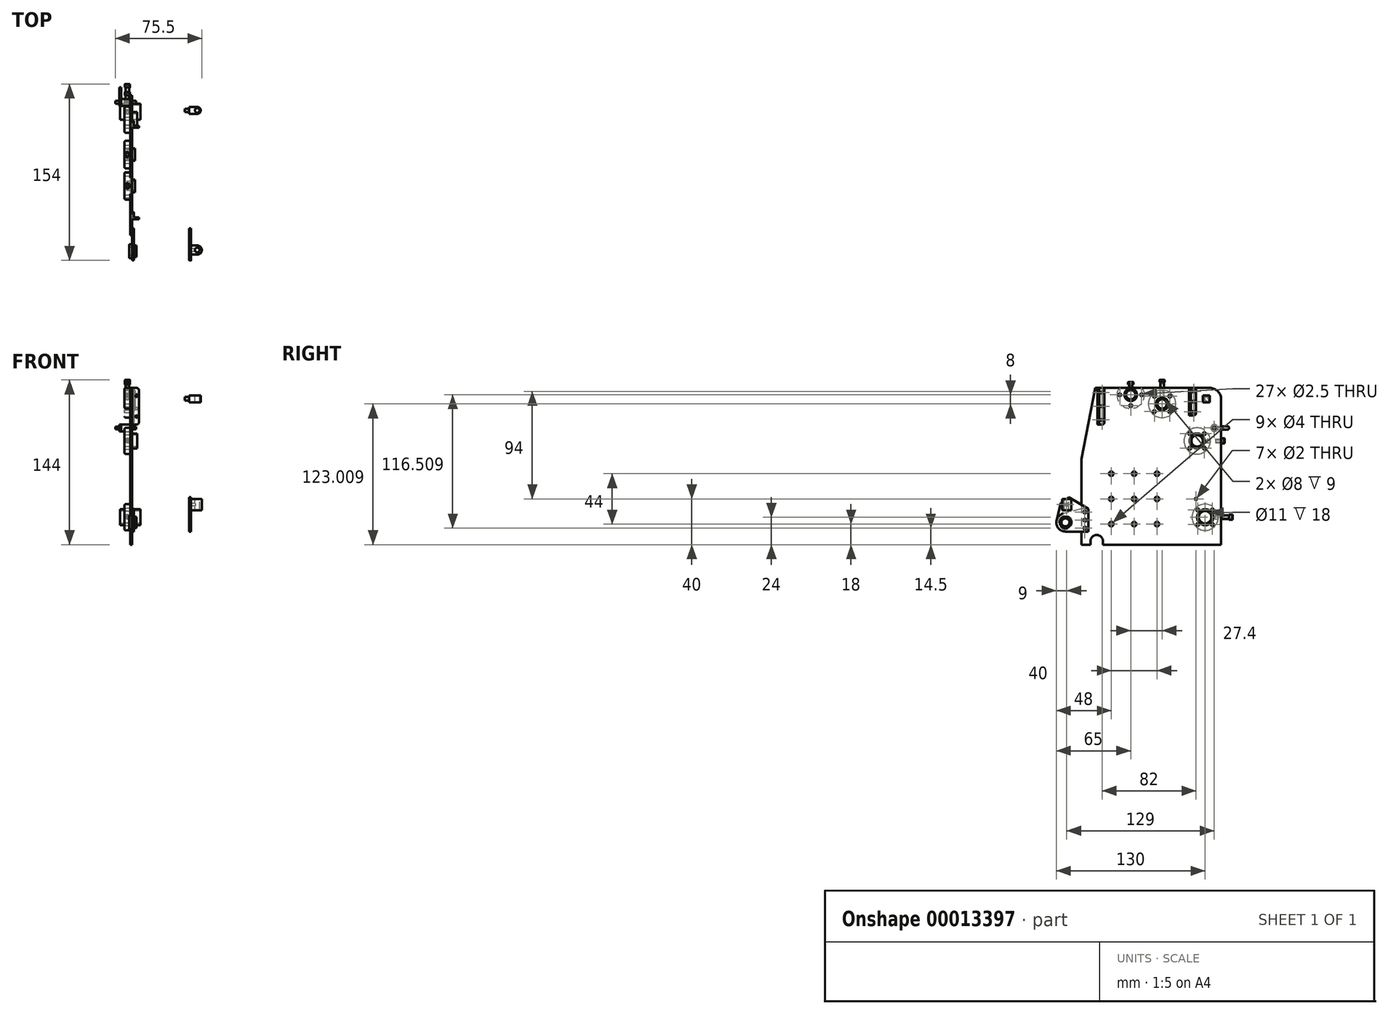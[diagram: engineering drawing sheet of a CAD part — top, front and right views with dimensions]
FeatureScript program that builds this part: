
annotation { "Feature Type Name" : "Feature", "Feature Type Description" : "" }
export const myFeature = defineFeature(function(context is Context, id is Id, definition is map)
    precondition{}
    {
        {
            var Q0;
            Q0=qCreatedBy(makeId("Right.planeOp"),FACE);
            var sketch = newSketch(context, id + "F0", { "sketchPlane" : qUnion([Q0])});
            skLineSegment(sketch, "E0", {"start": v(0, 75) * mm, "end": v(0, 0) * mm});
            skLineSegment(sketch, "E1", {"start": v(0, 0) * mm, "end": v(122, 0) * mm});
            skLineSegment(sketch, "E2", {"start": v(122, 0) * mm, "end": v(122, 127) * mm});
            skLineSegment(sketch, "E3", {"start": v(112, 137) * mm, "end": v(12, 137) * mm});
            skLineSegment(sketch, "E4", {"start": v(12, 137) * mm, "end": v(0, 75) * mm});
            skLineSegment(sketch, "E5", {"start": v(13.3, 0) * mm, "end": v(13.3, 3) * mm, "construction": true});
            skLineSegment(sketch, "E6", {"start": v(108, 0) * mm, "end": v(108, 24) * mm, "construction": true});
            skLineSegment(sketch, "E7", {"start": v(101, 0) * mm, "end": v(101, 90.7) * mm, "construction": true});
            skLineSegment(sketch, "E8", {"start": v(122, 40) * mm, "end": v(100, 40) * mm, "construction": true});
            skLineSegment(sketch, "E9", {"start": v(109, 137) * mm, "end": v(109, 127.5) * mm, "construction": true});
            skLineSegment(sketch, "E10", {"start": v(98, 137) * mm, "end": v(98, 134) * mm, "construction": true});
            skLineSegment(sketch, "E11", {"start": v(70.4, 137) * mm, "end": v(70.4, 101.73) * mm, "construction": true});
            skLineSegment(sketch, "E12", {"start": v(43, 137) * mm, "end": v(43, 131) * mm, "construction": true});
            skLineSegment(sketch, "E13", {"start": v(18, 137) * mm, "end": v(18, 133) * mm, "construction": true});
            skCircle(sketch, "E14", {"center": v(101, 90.7) * mm, "radius": 44.5 * mm, "construction": true});
            skCircle(sketch, "E15", {"center": v(70.4, 123) * mm, "radius": 5.5 * mm});
            skLineSegment(sketch, "E16", {"start": v(70.4, 123) * mm, "end": v(53.04, 123) * mm, "construction": true});
            skCircle(sketch, "E17", {"center": v(43, 131) * mm, "radius": 5.5 * mm});
            skCircle(sketch, "E18", {"center": v(101, 90.7) * mm, "radius": 6.5 * mm});
            skCircle(sketch, "E19", {"center": v(13.3, 3) * mm, "radius": 5.5 * mm});
            skCircle(sketch, "E20", {"center": v(108, 24) * mm, "radius": 7 * mm});
            skCircle(sketch, "E21", {"center": v(18, 133) * mm, "radius": 1 * mm});
            skCircle(sketch, "E22", {"center": v(98, 134) * mm, "radius": 1 * mm});
            skCircle(sketch, "E23", {"center": v(109, 127.5) * mm, "radius": 1.5 * mm});
            skCircle(sketch, "E24", {"center": v(100, 40) * mm, "radius": 1 * mm});
            skCircle(sketch, "E25.0.1.0", {"center": v(18, 121) * mm, "radius": 1 * mm});
            skCircle(sketch, "E25.0.2.0", {"center": v(18, 109) * mm, "radius": 1 * mm});
            skLineSegment(sketch, "E25.direction1", {"start": v(18, 133) * mm, "end": v(6, 133) * mm, "construction": true});
            skLineSegment(sketch, "E25.direction2", {"start": v(18, 133) * mm, "end": v(18, 121) * mm, "construction": true});
            skCircle(sketch, "E26.0.1.0", {"center": v(98, 125) * mm, "radius": 1 * mm});
            skCircle(sketch, "E26.0.2.0", {"center": v(98, 116) * mm, "radius": 1 * mm});
            skLineSegment(sketch, "E26.direction1", {"start": v(98, 134) * mm, "end": v(123, 134) * mm, "construction": true});
            skLineSegment(sketch, "E26.direction2", {"start": v(98, 134) * mm, "end": v(98, 125) * mm, "construction": true});
            skLineSegment(sketch, "E27", {"start": v(122, 102) * mm, "end": v(116, 102) * mm, "construction": true});
            skCircle(sketch, "E28", {"center": v(116, 102) * mm, "radius": 1.25 * mm});
            skLineSegment(sketch, "E29", {"start": v(43, 131) * mm, "end": v(33.5, 131) * mm, "construction": true});
            skCircle(sketch, "E30", {"center": v(33.5, 131) * mm, "radius": 1.25 * mm});
            skLineSegment(sketch, "E31", {"start": v(70.4, 123) * mm, "end": v(63.68, 129.73) * mm, "construction": true});
            skCircle(sketch, "E32", {"center": v(63.68, 129.73) * mm, "radius": 1.25 * mm});
            skCircle(sketch, "E33.1.0", {"center": v(63.68, 116.3) * mm, "radius": 1.25 * mm});
            skCircle(sketch, "E33.2.0", {"center": v(77.12, 116.3) * mm, "radius": 1.25 * mm});
            skCircle(sketch, "E33.3.0", {"center": v(77.12, 129.73) * mm, "radius": 1.25 * mm});
            skLineSegment(sketch, "E34", {"start": v(101, 90.7) * mm, "end": v(94.64, 84.34) * mm, "construction": true});
            skCircle(sketch, "E35", {"center": v(94.64, 84.34) * mm, "radius": 1.25 * mm});
            skCircle(sketch, "E36.1.0", {"center": v(107.36, 84.34) * mm, "radius": 1.25 * mm});
            skCircle(sketch, "E36.2.0", {"center": v(107.36, 97.06) * mm, "radius": 1.25 * mm});
            skCircle(sketch, "E36.3.0", {"center": v(94.64, 97.06) * mm, "radius": 1.25 * mm});
            skLineSegment(sketch, "E37", {"start": v(108, 24) * mm, "end": v(114.36, 17.64) * mm, "construction": true});
            skCircle(sketch, "E38", {"center": v(114.36, 17.64) * mm, "radius": 1.25 * mm});
            skCircle(sketch, "E39.1.0", {"center": v(114.36, 30.36) * mm, "radius": 1.25 * mm});
            skCircle(sketch, "E39.2.0", {"center": v(101.64, 30.36) * mm, "radius": 1.25 * mm});
            skCircle(sketch, "E39.3.0", {"center": v(101.64, 17.64) * mm, "radius": 1.25 * mm});
            skLineSegment(sketch, "E40", {"start": v(7.8, 3) * mm, "end": v(7.8, 0) * mm});
            skLineSegment(sketch, "E41", {"start": v(18.8, 3) * mm, "end": v(18.8, 0) * mm});
            skLineSegment(sketch, "E42", {"start": v(66, 0) * mm, "end": v(66, 18) * mm, "construction": true});
            skCircle(sketch, "E43", {"center": v(66, 18) * mm, "radius": 2 * mm});
            skCircle(sketch, "E44.0.1.0", {"center": v(66, 40) * mm, "radius": 2 * mm});
            skCircle(sketch, "E44.0.2.0", {"center": v(66, 62) * mm, "radius": 2 * mm});
            skCircle(sketch, "E44.1.0.0", {"center": v(46, 18) * mm, "radius": 2 * mm});
            skCircle(sketch, "E44.1.1.0", {"center": v(46, 40) * mm, "radius": 2 * mm});
            skCircle(sketch, "E44.1.2.0", {"center": v(46, 62) * mm, "radius": 2 * mm});
            skCircle(sketch, "E44.2.0.0", {"center": v(26, 18) * mm, "radius": 2 * mm});
            skCircle(sketch, "E44.2.1.0", {"center": v(26, 40) * mm, "radius": 2 * mm});
            skCircle(sketch, "E44.2.2.0", {"center": v(26, 62) * mm, "radius": 2 * mm});
            skLineSegment(sketch, "E44.direction1", {"start": v(66, 18) * mm, "end": v(46, 18) * mm, "construction": true});
            skLineSegment(sketch, "E44.direction2", {"start": v(66, 18) * mm, "end": v(66, 40) * mm, "construction": true});
            skLineSegment(sketch, "E45", {"start": v(0, 14.5) * mm, "end": v(3, 14.5) * mm, "construction": true});
            skCircle(sketch, "E46", {"center": v(3, 14.5) * mm, "radius": 1.25 * mm});
            skCircle(sketch, "E47.0.1.0", {"center": v(3, 21.5) * mm, "radius": 1.25 * mm});
            skCircle(sketch, "E47.0.2.0", {"center": v(3, 28.5) * mm, "radius": 1.25 * mm});
            skLineSegment(sketch, "E47.direction1", {"start": v(3, 14.5) * mm, "end": v(3, 14.5) * mm});
            skLineSegment(sketch, "E47.direction2", {"start": v(3, 14.5) * mm, "end": v(3, 21.5) * mm, "construction": true});
            skPoint(sketch, "E48.visualSharp", {"position": v(122, 137) * mm});
            skArc(sketch, "E48.filletArc", {"start": v(122, 127) * mm, "mid": v(119.07, 134.07) * mm, "end": v(112, 137) * mm});
            skCircle(sketch, "E49.1.0", {"center": v(43, 121.5) * mm, "radius": 1.25 * mm});
            skCircle(sketch, "E49.2.0", {"center": v(52.5, 131) * mm, "radius": 1.25 * mm});
            skCircle(sketch, "E49.3.0", {"center": v(43, 140.5) * mm, "radius": 1.25 * mm});
            skSolve(sketch);
        }
        {
            var Q0;
            {var subQ2=sQuery(id+"F0.wireOp",EDGE,"E0");Q0=makeQuery(id+"F0.imprint","IMPRINT",FACE,{"disambiguationData":[TD([[makeQuery(id+"F0.imprint","IMPRINT",EDGE,{"derivedFrom":subQ2}),1.0]])]});}
            extrude(context, id + "F1", {"entities" : qUnion([Q0]), "depth" : 1.5 * mm});
        }
        {
            var Q0;
            Q0=makeQuery(id+"F1.opExtrude","CAP_FACE",FACE,{"disambiguationData":[OSD([sQuery(id+"F0.wireOp",EDGE,"E0"),sQuery(id+"F0.wireOp",EDGE,"E1"),sQuery(id+"F0.wireOp",EDGE,"E2"),sQuery(id+"F0.wireOp",EDGE,"E3"),sQuery(id+"F0.wireOp",EDGE,"E4"),sQuery(id+"F0.wireOp",EDGE,"E15"),sQuery(id+"F0.wireOp",EDGE,"E17"),sQuery(id+"F0.wireOp",EDGE,"E18"),sQuery(id+"F0.wireOp",EDGE,"E19"),sQuery(id+"F0.wireOp",EDGE,"E20"),sQuery(id+"F0.wireOp",EDGE,"E21"),sQuery(id+"F0.wireOp",EDGE,"E22"),sQuery(id+"F0.wireOp",EDGE,"E23"),sQuery(id+"F0.wireOp",EDGE,"E24"),sQuery(id+"F0.wireOp",EDGE,"E25.0.1.0"),sQuery(id+"F0.wireOp",EDGE,"E25.0.2.0"),sQuery(id+"F0.wireOp",EDGE,"E26.0.1.0"),sQuery(id+"F0.wireOp",EDGE,"E26.0.2.0"),sQuery(id+"F0.wireOp",EDGE,"E28"),sQuery(id+"F0.wireOp",EDGE,"E30"),sQuery(id+"F0.wireOp",EDGE,"E32"),sQuery(id+"F0.wireOp",EDGE,"E33.1.0"),sQuery(id+"F0.wireOp",EDGE,"E33.2.0"),sQuery(id+"F0.wireOp",EDGE,"E33.3.0"),sQuery(id+"F0.wireOp",EDGE,"E35"),sQuery(id+"F0.wireOp",EDGE,"E36.1.0"),sQuery(id+"F0.wireOp",EDGE,"E36.2.0"),sQuery(id+"F0.wireOp",EDGE,"E36.3.0"),sQuery(id+"F0.wireOp",EDGE,"E38"),sQuery(id+"F0.wireOp",EDGE,"E39.1.0"),sQuery(id+"F0.wireOp",EDGE,"E39.2.0"),sQuery(id+"F0.wireOp",EDGE,"E39.3.0"),sQuery(id+"F0.wireOp",EDGE,"E40"),sQuery(id+"F0.wireOp",EDGE,"E41"),sQuery(id+"F0.wireOp",EDGE,"E43"),sQuery(id+"F0.wireOp",EDGE,"E44.0.1.0"),sQuery(id+"F0.wireOp",EDGE,"E44.0.2.0"),sQuery(id+"F0.wireOp",EDGE,"E44.1.0.0"),sQuery(id+"F0.wireOp",EDGE,"E44.1.1.0"),sQuery(id+"F0.wireOp",EDGE,"E44.1.2.0"),sQuery(id+"F0.wireOp",EDGE,"E44.2.0.0"),sQuery(id+"F0.wireOp",EDGE,"E44.2.1.0"),sQuery(id+"F0.wireOp",EDGE,"E44.2.2.0"),sQuery(id+"F0.wireOp",EDGE,"E46"),sQuery(id+"F0.wireOp",EDGE,"E47.0.1.0"),sQuery(id+"F0.wireOp",EDGE,"E47.0.2.0"),sQuery(id+"F0.wireOp",EDGE,"E48.filletArc"),sQuery(id+"F0.wireOp",EDGE,"E49.1.0"),sQuery(id+"F0.wireOp",EDGE,"E49.2.0")])],"isStart":false});
            var sketch = newSketch(context, id + "F2", { "sketchPlane" : qUnion([Q0])});
            skCircle(sketch, "E50.0", {"center": v(18, 133) * mm, "radius": 1 * mm});
            skCircle(sketch, "E50.1", {"center": v(18, 121) * mm, "radius": 1 * mm});
            skCircle(sketch, "E50.2", {"center": v(18, 109) * mm, "radius": 1 * mm});
            skLineSegment(sketch, "E51.bottom", {"start": v(14, 137) * mm, "end": v(18, 137) * mm});
            skLineSegment(sketch, "E51.top", {"start": v(14, 105) * mm, "end": v(18, 105) * mm});
            skLineSegment(sketch, "E51.left", {"start": v(14, 137) * mm, "end": v(14, 105) * mm});
            skLineSegment(sketch, "E51.right", {"start": v(20, 135) * mm, "end": v(20, 107) * mm});
            skLineSegment(sketch, "E52", {"start": v(15.5, 137) * mm, "end": v(15.5, 105) * mm});
            skPoint(sketch, "E53.visualSharp", {"position": v(20, 137) * mm});
            skArc(sketch, "E53.filletArc", {"start": v(20, 135) * mm, "mid": v(19.41, 136.41) * mm, "end": v(18, 137) * mm});
            skPoint(sketch, "E54.visualSharp", {"position": v(20, 105) * mm});
            skArc(sketch, "E54.filletArc", {"start": v(18, 105) * mm, "mid": v(19.41, 105.59) * mm, "end": v(20, 107) * mm});
            skSolve(sketch);
        }
        {
            var Q0;
            {var subQ1=sQuery(id+"F2.wireOp",EDGE,"E51.left");Q0=makeQuery(id+"F2.imprint","IMPRINT",FACE,{"disambiguationData":[TD([[makeQuery(id+"F2.imprint","IMPRINT",EDGE,{"derivedFrom":subQ1}),1.0]])]});}
            extrude(context, id + "F3", {"entities" : qUnion([Q0]), "depth" : 6 * mm});
        }
        {
            var Q0;
            Q0=makeQuery(id+"F2.imprint","IMPRINT",FACE,{"disambiguationData":[TD([[makeQuery(id+"F2.imprint","IMPRINT",EDGE,{"derivedFrom":sQuery(id+"F2.wireOp",EDGE,"E50.0")}),-1.0]])]});
            extrude(context, id + "F4", {"entities" : qUnion([Q0]), "operationType" : NewBodyOperationType.ADD, "depth" : 1.5 * mm});
        }
        {
            var Q0;
            Q0=makeQuery(id+"F3.opExtrude","SWEPT_FACE",FACE,{"disambiguationData":[OSD([sQuery(id+"F2.wireOp",EDGE,"E51.left")])]});
            var sketch = newSketch(context, id + "F5", { "sketchPlane" : qUnion([Q0])});
            skLineSegment(sketch, "E55", {"start": v(5.5, 137) * mm, "end": v(5.5, 105) * mm, "construction": true});
            skLineSegment(sketch, "E56", {"start": v(5.5, 130) * mm, "end": v(7.5, 130) * mm, "construction": true});
            skLineSegment(sketch, "E57", {"start": v(5.5, 112) * mm, "end": v(7.5, 112) * mm, "construction": true});
            skCircle(sketch, "E58", {"center": v(5.5, 130) * mm, "radius": 1 * mm});
            skCircle(sketch, "E59", {"center": v(5.5, 112) * mm, "radius": 1 * mm});
            skSolve(sketch);
        }
        {
            var Q0;
            Q0=makeQuery(id+"F5.imprint","IMPRINT",FACE,{"disambiguationData":[TD([[makeQuery(id+"F5.imprint","IMPRINT",EDGE,{"derivedFrom":sQuery(id+"F5.wireOp",EDGE,"E58")}),1.0]])]});
            var Q1;
            Q1=makeQuery(id+"F5.imprint","IMPRINT",FACE,{"disambiguationData":[TD([[makeQuery(id+"F5.imprint","IMPRINT",EDGE,{"derivedFrom":sQuery(id+"F5.wireOp",EDGE,"E59")}),1.0]])]});
            extrude(context, id + "F6", {"entities" : qUnion([Q0, Q1]), "operationType" : NewBodyOperationType.REMOVE, "oppositeDirection" : true, "depth" : 1.5 * mm});
        }
        {
            var Q0;
            Q0=makeQuery(id+"F3.opExtrude","CAP_EDGE",EDGE,{"disambiguationData":[OSD([sQuery(id+"F2.wireOp",EDGE,"E51.bottom")])],"isStart":false});
            var Q1;
            Q1=makeQuery(id+"F3.opExtrude","CAP_EDGE",EDGE,{"disambiguationData":[OSD([sQuery(id+"F2.wireOp",EDGE,"E51.top")])],"isStart":false});
            fillet(context, id + "F7", {"entities" : qUnion([Q0, Q1]), "radius" : 2 * mm, "tangentPropagation" : true, "allowEdgeOverflow" : false});
        }
        {
            var Q0;
            Q0=makeQuery(id+"F1.opExtrude","CAP_FACE",FACE,{"disambiguationData":[OSD([sQuery(id+"F0.wireOp",EDGE,"E0"),sQuery(id+"F0.wireOp",EDGE,"E1"),sQuery(id+"F0.wireOp",EDGE,"E2"),sQuery(id+"F0.wireOp",EDGE,"E3"),sQuery(id+"F0.wireOp",EDGE,"E4"),sQuery(id+"F0.wireOp",EDGE,"E15"),sQuery(id+"F0.wireOp",EDGE,"E17"),sQuery(id+"F0.wireOp",EDGE,"E18"),sQuery(id+"F0.wireOp",EDGE,"E19"),sQuery(id+"F0.wireOp",EDGE,"E20"),sQuery(id+"F0.wireOp",EDGE,"E21"),sQuery(id+"F0.wireOp",EDGE,"E22"),sQuery(id+"F0.wireOp",EDGE,"E23"),sQuery(id+"F0.wireOp",EDGE,"E24"),sQuery(id+"F0.wireOp",EDGE,"E25.0.1.0"),sQuery(id+"F0.wireOp",EDGE,"E25.0.2.0"),sQuery(id+"F0.wireOp",EDGE,"E26.0.1.0"),sQuery(id+"F0.wireOp",EDGE,"E26.0.2.0"),sQuery(id+"F0.wireOp",EDGE,"E28"),sQuery(id+"F0.wireOp",EDGE,"E30"),sQuery(id+"F0.wireOp",EDGE,"E32"),sQuery(id+"F0.wireOp",EDGE,"E33.1.0"),sQuery(id+"F0.wireOp",EDGE,"E33.2.0"),sQuery(id+"F0.wireOp",EDGE,"E33.3.0"),sQuery(id+"F0.wireOp",EDGE,"E35"),sQuery(id+"F0.wireOp",EDGE,"E36.1.0"),sQuery(id+"F0.wireOp",EDGE,"E36.2.0"),sQuery(id+"F0.wireOp",EDGE,"E36.3.0"),sQuery(id+"F0.wireOp",EDGE,"E38"),sQuery(id+"F0.wireOp",EDGE,"E39.1.0"),sQuery(id+"F0.wireOp",EDGE,"E39.2.0"),sQuery(id+"F0.wireOp",EDGE,"E39.3.0"),sQuery(id+"F0.wireOp",EDGE,"E40"),sQuery(id+"F0.wireOp",EDGE,"E41"),sQuery(id+"F0.wireOp",EDGE,"E43"),sQuery(id+"F0.wireOp",EDGE,"E44.0.1.0"),sQuery(id+"F0.wireOp",EDGE,"E44.0.2.0"),sQuery(id+"F0.wireOp",EDGE,"E44.1.0.0"),sQuery(id+"F0.wireOp",EDGE,"E44.1.1.0"),sQuery(id+"F0.wireOp",EDGE,"E44.1.2.0"),sQuery(id+"F0.wireOp",EDGE,"E44.2.0.0"),sQuery(id+"F0.wireOp",EDGE,"E44.2.1.0"),sQuery(id+"F0.wireOp",EDGE,"E44.2.2.0"),sQuery(id+"F0.wireOp",EDGE,"E46"),sQuery(id+"F0.wireOp",EDGE,"E47.0.1.0"),sQuery(id+"F0.wireOp",EDGE,"E47.0.2.0"),sQuery(id+"F0.wireOp",EDGE,"E48.filletArc"),sQuery(id+"F0.wireOp",EDGE,"E49.1.0"),sQuery(id+"F0.wireOp",EDGE,"E49.2.0")])],"isStart":false});
            var sketch = newSketch(context, id + "F8", { "sketchPlane" : qUnion([Q0])});
            skCircle(sketch, "E60.0", {"center": v(98, 134) * mm, "radius": 1 * mm});
            skCircle(sketch, "E60.1", {"center": v(98, 125) * mm, "radius": 1 * mm});
            skCircle(sketch, "E60.2", {"center": v(98, 116) * mm, "radius": 1 * mm});
            skLineSegment(sketch, "E61.bottom", {"start": v(98, 137) * mm, "end": v(94, 137) * mm});
            skLineSegment(sketch, "E61.top", {"start": v(98, 113) * mm, "end": v(94, 113) * mm});
            skLineSegment(sketch, "E61.left", {"start": v(100, 135) * mm, "end": v(100, 115) * mm});
            skLineSegment(sketch, "E61.right", {"start": v(94, 137) * mm, "end": v(94, 113) * mm});
            skLineSegment(sketch, "E62", {"start": v(95.5, 137) * mm, "end": v(95.5, 113) * mm});
            skPoint(sketch, "E63.visualSharp", {"position": v(100, 113) * mm});
            skArc(sketch, "E63.filletArc", {"start": v(98, 113) * mm, "mid": v(99.41, 113.59) * mm, "end": v(100, 115) * mm});
            skPoint(sketch, "E64.visualSharp", {"position": v(100, 137) * mm});
            skArc(sketch, "E64.filletArc", {"start": v(100, 135) * mm, "mid": v(99.41, 136.41) * mm, "end": v(98, 137) * mm});
            skSolve(sketch);
        }
        {
            var Q0;
            {var subQ1=sQuery(id+"F8.wireOp",EDGE,"E61.right");Q0=makeQuery(id+"F8.imprint","IMPRINT",FACE,{"disambiguationData":[TD([[makeQuery(id+"F8.imprint","IMPRINT",EDGE,{"derivedFrom":subQ1}),1.0]])]});}
            extrude(context, id + "F9", {"entities" : qUnion([Q0]), "depth" : 6 * mm});
        }
        {
            var Q0;
            Q0=makeQuery(id+"F8.imprint","IMPRINT",FACE,{"disambiguationData":[TD([[makeQuery(id+"F8.imprint","IMPRINT",EDGE,{"derivedFrom":sQuery(id+"F8.wireOp",EDGE,"E60.0")}),-1.0]])]});
            extrude(context, id + "F10", {"entities" : qUnion([Q0]), "operationType" : NewBodyOperationType.ADD, "depth" : 1.5 * mm});
        }
        {
            var Q0;
            Q0=makeQuery(id+"F9.opExtrude","SWEPT_FACE",FACE,{"disambiguationData":[OSD([sQuery(id+"F8.wireOp",EDGE,"E61.right")])]});
            var sketch = newSketch(context, id + "F11", { "sketchPlane" : qUnion([Q0])});
            skLineSegment(sketch, "E65", {"start": v(5.5, 137) * mm, "end": v(5.5, 113) * mm, "construction": true});
            skLineSegment(sketch, "E66", {"start": v(5.5, 131) * mm, "end": v(7.5, 131) * mm, "construction": true});
            skLineSegment(sketch, "E67", {"start": v(5.5, 119) * mm, "end": v(7.5, 119) * mm, "construction": true});
            skCircle(sketch, "E68", {"center": v(5.5, 131) * mm, "radius": 1 * mm});
            skCircle(sketch, "E69", {"center": v(5.5, 119) * mm, "radius": 1 * mm});
            skSolve(sketch);
        }
        {
            var Q0;
            Q0=makeQuery(id+"F11.imprint","IMPRINT",FACE,{"disambiguationData":[TD([[makeQuery(id+"F11.imprint","IMPRINT",EDGE,{"derivedFrom":sQuery(id+"F11.wireOp",EDGE,"E68")}),1.0]])]});
            var Q1;
            Q1=makeQuery(id+"F11.imprint","IMPRINT",FACE,{"disambiguationData":[TD([[makeQuery(id+"F11.imprint","IMPRINT",EDGE,{"derivedFrom":sQuery(id+"F11.wireOp",EDGE,"E69")}),1.0]])]});
            extrude(context, id + "F12", {"entities" : qUnion([Q0, Q1]), "operationType" : NewBodyOperationType.REMOVE, "oppositeDirection" : true, "depth" : 1.5 * mm});
        }
        {
            var Q0;
            Q0=makeQuery(id+"F9.opExtrude","CAP_EDGE",EDGE,{"disambiguationData":[OSD([sQuery(id+"F8.wireOp",EDGE,"E61.bottom")])],"isStart":false});
            var Q1;
            Q1=makeQuery(id+"F9.opExtrude","CAP_EDGE",EDGE,{"disambiguationData":[OSD([sQuery(id+"F8.wireOp",EDGE,"E61.top")])],"isStart":false});
            fillet(context, id + "F13", {"entities" : qUnion([Q0, Q1]), "radius" : 2 * mm, "tangentPropagation" : true, "allowEdgeOverflow" : false});
        }
        {
            var Q0;
            Q0=makeQuery(id+"F1.opExtrude","CAP_FACE",FACE,{"disambiguationData":[OSD([sQuery(id+"F0.wireOp",EDGE,"E0"),sQuery(id+"F0.wireOp",EDGE,"E1"),sQuery(id+"F0.wireOp",EDGE,"E2"),sQuery(id+"F0.wireOp",EDGE,"E3"),sQuery(id+"F0.wireOp",EDGE,"E4"),sQuery(id+"F0.wireOp",EDGE,"E15"),sQuery(id+"F0.wireOp",EDGE,"E17"),sQuery(id+"F0.wireOp",EDGE,"E18"),sQuery(id+"F0.wireOp",EDGE,"E19"),sQuery(id+"F0.wireOp",EDGE,"E20"),sQuery(id+"F0.wireOp",EDGE,"E21"),sQuery(id+"F0.wireOp",EDGE,"E22"),sQuery(id+"F0.wireOp",EDGE,"E23"),sQuery(id+"F0.wireOp",EDGE,"E24"),sQuery(id+"F0.wireOp",EDGE,"E25.0.1.0"),sQuery(id+"F0.wireOp",EDGE,"E25.0.2.0"),sQuery(id+"F0.wireOp",EDGE,"E26.0.1.0"),sQuery(id+"F0.wireOp",EDGE,"E26.0.2.0"),sQuery(id+"F0.wireOp",EDGE,"E28"),sQuery(id+"F0.wireOp",EDGE,"E30"),sQuery(id+"F0.wireOp",EDGE,"E32"),sQuery(id+"F0.wireOp",EDGE,"E33.1.0"),sQuery(id+"F0.wireOp",EDGE,"E33.2.0"),sQuery(id+"F0.wireOp",EDGE,"E33.3.0"),sQuery(id+"F0.wireOp",EDGE,"E35"),sQuery(id+"F0.wireOp",EDGE,"E36.1.0"),sQuery(id+"F0.wireOp",EDGE,"E36.2.0"),sQuery(id+"F0.wireOp",EDGE,"E36.3.0"),sQuery(id+"F0.wireOp",EDGE,"E38"),sQuery(id+"F0.wireOp",EDGE,"E39.1.0"),sQuery(id+"F0.wireOp",EDGE,"E39.2.0"),sQuery(id+"F0.wireOp",EDGE,"E39.3.0"),sQuery(id+"F0.wireOp",EDGE,"E40"),sQuery(id+"F0.wireOp",EDGE,"E41"),sQuery(id+"F0.wireOp",EDGE,"E43"),sQuery(id+"F0.wireOp",EDGE,"E44.0.1.0"),sQuery(id+"F0.wireOp",EDGE,"E44.0.2.0"),sQuery(id+"F0.wireOp",EDGE,"E44.1.0.0"),sQuery(id+"F0.wireOp",EDGE,"E44.1.1.0"),sQuery(id+"F0.wireOp",EDGE,"E44.1.2.0"),sQuery(id+"F0.wireOp",EDGE,"E44.2.0.0"),sQuery(id+"F0.wireOp",EDGE,"E44.2.1.0"),sQuery(id+"F0.wireOp",EDGE,"E44.2.2.0"),sQuery(id+"F0.wireOp",EDGE,"E46"),sQuery(id+"F0.wireOp",EDGE,"E47.0.1.0"),sQuery(id+"F0.wireOp",EDGE,"E47.0.2.0"),sQuery(id+"F0.wireOp",EDGE,"E48.filletArc"),sQuery(id+"F0.wireOp",EDGE,"E49.1.0"),sQuery(id+"F0.wireOp",EDGE,"E49.2.0")])],"isStart":true});
            var sketch = newSketch(context, id + "F14", { "sketchPlane" : qUnion([Q0])});
            skCircle(sketch, "E70.0", {"center": v(-43, 131) * mm, "radius": 5.5 * mm});
            skCircle(sketch, "E70.1", {"center": v(-43, 121.5) * mm, "radius": 1.25 * mm});
            skCircle(sketch, "E70.2", {"center": v(-52.5, 131) * mm, "radius": 1.25 * mm});
            skCircle(sketch, "E70.3", {"center": v(-33.5, 131) * mm, "radius": 1.25 * mm});
            skCircle(sketch, "E71", {"center": v(-43, 131) * mm, "radius": 12 * mm});
            skCircle(sketch, "E72", {"center": v(-43, 131) * mm, "radius": 4 * mm});
            skSolve(sketch);
        }
        {
            var Q0;
            Q0=makeQuery(id+"F14.imprint","IMPRINT",FACE,{"disambiguationData":[TD([[makeQuery(id+"F14.imprint","IMPRINT",EDGE,{"derivedFrom":sQuery(id+"F14.wireOp",EDGE,"E70.0")}),-1.0]])]});
            extrude(context, id + "F15", {"entities" : qUnion([Q0]), "oppositeDirection" : true, "depth" : 4 * mm});
        }
        {
            var Q0;
            Q0=makeQuery(id+"F14.imprint","IMPRINT",FACE,{"disambiguationData":[TD([[makeQuery(id+"F14.imprint","IMPRINT",EDGE,{"derivedFrom":sQuery(id+"F14.wireOp",EDGE,"E70.0")}),1.0]])]});
            var Q1;
            Q1=makeQuery(id+"F14.imprint","IMPRINT",FACE,{"disambiguationData":[TD([[makeQuery(id+"F14.imprint","IMPRINT",EDGE,{"derivedFrom":sQuery(id+"F14.wireOp",EDGE,"E70.0")}),-1.0]])]});
            extrude(context, id + "F16", {"entities" : qUnion([Q0, Q1]), "operationType" : NewBodyOperationType.ADD, "depth" : 5 * mm});
        }
        {
            var Q0;
            Q0=makeQuery(id+"F16.opExtrude","SWEPT_FACE",FACE,{"disambiguationData":[OSD([sQuery(id+"F0.wireOp",EDGE,"E3")])]});
            var sketch = newSketch(context, id + "F17", { "sketchPlane" : qUnion([Q0])});
            skLineSegment(sketch, "E73", {"start": v(-5, 43) * mm, "end": v(0, 43) * mm, "construction": true});
            skCircle(sketch, "E74", {"center": v(-2.5, 43) * mm, "radius": 1.5 * mm});
            skCircle(sketch, "E75", {"center": v(-2.5, 43) * mm, "radius": 0.75 * mm});
            skSolve(sketch);
        }
        {
            var Q0;
            Q0=makeQuery(id+"F17.imprint","IMPRINT",FACE,{"disambiguationData":[TD([[makeQuery(id+"F17.imprint","IMPRINT",EDGE,{"derivedFrom":sQuery(id+"F17.wireOp",EDGE,"E75")}),1.0]])]});
            extrude(context, id + "F18", {"entities" : qUnion([Q0]), "operationType" : NewBodyOperationType.REMOVE, "oppositeDirection" : true, "depth" : 6 * mm});
        }
        {
            var Q0;
            Q0=makeQuery(id+"F17.imprint","IMPRINT",FACE,{"disambiguationData":[TD([[makeQuery(id+"F17.imprint","IMPRINT",EDGE,{"derivedFrom":sQuery(id+"F17.wireOp",EDGE,"E74")}),1.0]])]});
            extrude(context, id + "F19", {"entities" : qUnion([Q0]), "operationType" : NewBodyOperationType.REMOVE, "oppositeDirection" : true, "depth" : 1.5 * mm});
        }
        {
            var Q0;
            {var subQ0=sQuery(id+"F0.wireOp",EDGE,"E3");var subQ1=sQuery(id+"F14.wireOp",EDGE,"E71");Q0=makeQuery(id+"F16.opExtrude","SWEPT_EDGE",EDGE,{"disambiguationData":[OSD([subQ0,subQ1]),TDD([makeQuery(id+"F14.imprint","INTERSECT",VERTEX,{"disambiguationData":[OD(0.0)],"derivedFrom":[makeQuery(id+"F1.opExtrude","CAP_EDGE",EDGE,{"disambiguationData":[OSD([subQ0])],"isStart":true}),subQ1]})])]});}
            var Q1;
            {var subQ0=sQuery(id+"F0.wireOp",EDGE,"E3");var subQ1=sQuery(id+"F14.wireOp",EDGE,"E71");Q1=makeQuery(id+"F16.opExtrude","SWEPT_EDGE",EDGE,{"disambiguationData":[OSD([subQ0,subQ1]),TDD([makeQuery(id+"F14.imprint","INTERSECT",VERTEX,{"disambiguationData":[OD(1.0)],"derivedFrom":[makeQuery(id+"F1.opExtrude","CAP_EDGE",EDGE,{"disambiguationData":[OSD([subQ0])],"isStart":true}),subQ1]})])]});}
            fillet(context, id + "F20", {"entities" : qUnion([Q0, Q1]), "radius" : 5 * mm, "tangentPropagation" : true, "allowEdgeOverflow" : false});
        }
        {
            var Q0;
            Q0=makeQuery(id+"F1.opExtrude","CAP_FACE",FACE,{"disambiguationData":[OSD([sQuery(id+"F0.wireOp",EDGE,"E0"),sQuery(id+"F0.wireOp",EDGE,"E1"),sQuery(id+"F0.wireOp",EDGE,"E2"),sQuery(id+"F0.wireOp",EDGE,"E3"),sQuery(id+"F0.wireOp",EDGE,"E4"),sQuery(id+"F0.wireOp",EDGE,"E15"),sQuery(id+"F0.wireOp",EDGE,"E17"),sQuery(id+"F0.wireOp",EDGE,"E18"),sQuery(id+"F0.wireOp",EDGE,"E19"),sQuery(id+"F0.wireOp",EDGE,"E20"),sQuery(id+"F0.wireOp",EDGE,"E21"),sQuery(id+"F0.wireOp",EDGE,"E22"),sQuery(id+"F0.wireOp",EDGE,"E23"),sQuery(id+"F0.wireOp",EDGE,"E24"),sQuery(id+"F0.wireOp",EDGE,"E25.0.1.0"),sQuery(id+"F0.wireOp",EDGE,"E25.0.2.0"),sQuery(id+"F0.wireOp",EDGE,"E26.0.1.0"),sQuery(id+"F0.wireOp",EDGE,"E26.0.2.0"),sQuery(id+"F0.wireOp",EDGE,"E28"),sQuery(id+"F0.wireOp",EDGE,"E30"),sQuery(id+"F0.wireOp",EDGE,"E32"),sQuery(id+"F0.wireOp",EDGE,"E33.1.0"),sQuery(id+"F0.wireOp",EDGE,"E33.2.0"),sQuery(id+"F0.wireOp",EDGE,"E33.3.0"),sQuery(id+"F0.wireOp",EDGE,"E35"),sQuery(id+"F0.wireOp",EDGE,"E36.1.0"),sQuery(id+"F0.wireOp",EDGE,"E36.2.0"),sQuery(id+"F0.wireOp",EDGE,"E36.3.0"),sQuery(id+"F0.wireOp",EDGE,"E38"),sQuery(id+"F0.wireOp",EDGE,"E39.1.0"),sQuery(id+"F0.wireOp",EDGE,"E39.2.0"),sQuery(id+"F0.wireOp",EDGE,"E39.3.0"),sQuery(id+"F0.wireOp",EDGE,"E40"),sQuery(id+"F0.wireOp",EDGE,"E41"),sQuery(id+"F0.wireOp",EDGE,"E43"),sQuery(id+"F0.wireOp",EDGE,"E44.0.1.0"),sQuery(id+"F0.wireOp",EDGE,"E44.0.2.0"),sQuery(id+"F0.wireOp",EDGE,"E44.1.0.0"),sQuery(id+"F0.wireOp",EDGE,"E44.1.1.0"),sQuery(id+"F0.wireOp",EDGE,"E44.1.2.0"),sQuery(id+"F0.wireOp",EDGE,"E44.2.0.0"),sQuery(id+"F0.wireOp",EDGE,"E44.2.1.0"),sQuery(id+"F0.wireOp",EDGE,"E44.2.2.0"),sQuery(id+"F0.wireOp",EDGE,"E46"),sQuery(id+"F0.wireOp",EDGE,"E47.0.1.0"),sQuery(id+"F0.wireOp",EDGE,"E47.0.2.0"),sQuery(id+"F0.wireOp",EDGE,"E48.filletArc"),sQuery(id+"F0.wireOp",EDGE,"E49.1.0"),sQuery(id+"F0.wireOp",EDGE,"E49.2.0")])],"isStart":true});
            var sketch = newSketch(context, id + "F21", { "sketchPlane" : qUnion([Q0])});
            skCircle(sketch, "E76.0", {"center": v(-77.12, 129.73) * mm, "radius": 1.25 * mm});
            skCircle(sketch, "E76.1", {"center": v(-63.68, 129.73) * mm, "radius": 1.25 * mm});
            skCircle(sketch, "E76.2", {"center": v(-63.68, 116.3) * mm, "radius": 1.25 * mm});
            skCircle(sketch, "E76.3", {"center": v(-77.12, 116.3) * mm, "radius": 1.25 * mm});
            skCircle(sketch, "E76.4", {"center": v(-70.4, 123) * mm, "radius": 5.5 * mm});
            skCircle(sketch, "E77", {"center": v(-70.4, 123) * mm, "radius": 12 * mm});
            skCircle(sketch, "E78", {"center": v(-70.4, 123) * mm, "radius": 4 * mm});
            skSolve(sketch);
        }
        {
            var Q0;
            Q0=makeQuery(id+"F21.imprint","IMPRINT",FACE,{"disambiguationData":[TD([[makeQuery(id+"F21.imprint","IMPRINT",EDGE,{"derivedFrom":sQuery(id+"F21.wireOp",EDGE,"E76.4")}),-1.0]])]});
            extrude(context, id + "F22", {"entities" : qUnion([Q0]), "oppositeDirection" : true, "depth" : 4 * mm});
        }
        {
            var Q0;
            Q0=makeQuery(id+"F21.imprint","IMPRINT",FACE,{"disambiguationData":[TD([[makeQuery(id+"F21.imprint","IMPRINT",EDGE,{"derivedFrom":sQuery(id+"F21.wireOp",EDGE,"E76.0")}),1.0]])]});
            var Q1;
            Q1=makeQuery(id+"F21.imprint","IMPRINT",FACE,{"disambiguationData":[TD([[makeQuery(id+"F21.imprint","IMPRINT",EDGE,{"derivedFrom":sQuery(id+"F21.wireOp",EDGE,"E76.4")}),-1.0]])]});
            extrude(context, id + "F23", {"entities" : qUnion([Q0, Q1]), "operationType" : NewBodyOperationType.ADD, "depth" : 5 * mm});
        }
        {
            var Q0;
            Q0=makeQuery(id+"F1.opExtrude","SWEPT_FACE",FACE,{"disambiguationData":[OSD([sQuery(id+"F0.wireOp",EDGE,"E3")])]});
            var sketch = newSketch(context, id + "F24", { "sketchPlane" : qUnion([Q0])});
            skLineSegment(sketch, "E79.0", {"start": v(-5, 58.4) * mm, "end": v(-5, 82.4) * mm, "construction": true});
            skLineSegment(sketch, "E80", {"start": v(-5, 70.4) * mm, "end": v(0, 70.4) * mm, "construction": true});
            skCircle(sketch, "E81", {"center": v(-2.5, 70.4) * mm, "radius": 1.5 * mm});
            skSolve(sketch);
        }
        {
            var Q0;
            Q0=makeQuery(id+"F24.imprint","IMPRINT",FACE,{"disambiguationData":[TD([[makeQuery(id+"F24.imprint","IMPRINT",EDGE,{"derivedFrom":sQuery(id+"F24.wireOp",EDGE,"E81")}),1.0]])]});
            extrude(context, id + "F25", {"entities" : qUnion([Q0]), "operationType" : NewBodyOperationType.REMOVE, "oppositeDirection" : true, "depth" : 12 * mm});
        }
        {
            var Q0;
            Q0=makeQuery(id+"F1.opExtrude","CAP_FACE",FACE,{"disambiguationData":[OSD([sQuery(id+"F0.wireOp",EDGE,"E0"),sQuery(id+"F0.wireOp",EDGE,"E1"),sQuery(id+"F0.wireOp",EDGE,"E2"),sQuery(id+"F0.wireOp",EDGE,"E3"),sQuery(id+"F0.wireOp",EDGE,"E4"),sQuery(id+"F0.wireOp",EDGE,"E15"),sQuery(id+"F0.wireOp",EDGE,"E17"),sQuery(id+"F0.wireOp",EDGE,"E18"),sQuery(id+"F0.wireOp",EDGE,"E19"),sQuery(id+"F0.wireOp",EDGE,"E20"),sQuery(id+"F0.wireOp",EDGE,"E21"),sQuery(id+"F0.wireOp",EDGE,"E22"),sQuery(id+"F0.wireOp",EDGE,"E23"),sQuery(id+"F0.wireOp",EDGE,"E24"),sQuery(id+"F0.wireOp",EDGE,"E25.0.1.0"),sQuery(id+"F0.wireOp",EDGE,"E25.0.2.0"),sQuery(id+"F0.wireOp",EDGE,"E26.0.1.0"),sQuery(id+"F0.wireOp",EDGE,"E26.0.2.0"),sQuery(id+"F0.wireOp",EDGE,"E28"),sQuery(id+"F0.wireOp",EDGE,"E30"),sQuery(id+"F0.wireOp",EDGE,"E32"),sQuery(id+"F0.wireOp",EDGE,"E33.1.0"),sQuery(id+"F0.wireOp",EDGE,"E33.2.0"),sQuery(id+"F0.wireOp",EDGE,"E33.3.0"),sQuery(id+"F0.wireOp",EDGE,"E35"),sQuery(id+"F0.wireOp",EDGE,"E36.1.0"),sQuery(id+"F0.wireOp",EDGE,"E36.2.0"),sQuery(id+"F0.wireOp",EDGE,"E36.3.0"),sQuery(id+"F0.wireOp",EDGE,"E38"),sQuery(id+"F0.wireOp",EDGE,"E39.1.0"),sQuery(id+"F0.wireOp",EDGE,"E39.2.0"),sQuery(id+"F0.wireOp",EDGE,"E39.3.0"),sQuery(id+"F0.wireOp",EDGE,"E40"),sQuery(id+"F0.wireOp",EDGE,"E41"),sQuery(id+"F0.wireOp",EDGE,"E43"),sQuery(id+"F0.wireOp",EDGE,"E44.0.1.0"),sQuery(id+"F0.wireOp",EDGE,"E44.0.2.0"),sQuery(id+"F0.wireOp",EDGE,"E44.1.0.0"),sQuery(id+"F0.wireOp",EDGE,"E44.1.1.0"),sQuery(id+"F0.wireOp",EDGE,"E44.1.2.0"),sQuery(id+"F0.wireOp",EDGE,"E44.2.0.0"),sQuery(id+"F0.wireOp",EDGE,"E44.2.1.0"),sQuery(id+"F0.wireOp",EDGE,"E44.2.2.0"),sQuery(id+"F0.wireOp",EDGE,"E46"),sQuery(id+"F0.wireOp",EDGE,"E47.0.1.0"),sQuery(id+"F0.wireOp",EDGE,"E47.0.2.0"),sQuery(id+"F0.wireOp",EDGE,"E48.filletArc"),sQuery(id+"F0.wireOp",EDGE,"E49.1.0"),sQuery(id+"F0.wireOp",EDGE,"E49.2.0")])],"isStart":true});
            var sketch = newSketch(context, id + "F26", { "sketchPlane" : qUnion([Q0])});
            skCircle(sketch, "E82.0", {"center": v(-107.36, 84.34) * mm, "radius": 1.25 * mm});
            skCircle(sketch, "E82.1", {"center": v(-107.36, 97.06) * mm, "radius": 1.25 * mm});
            skCircle(sketch, "E82.2", {"center": v(-94.64, 97.06) * mm, "radius": 1.25 * mm});
            skCircle(sketch, "E82.3", {"center": v(-94.64, 84.34) * mm, "radius": 1.25 * mm});
            skCircle(sketch, "E82.4", {"center": v(-101, 90.7) * mm, "radius": 6.5 * mm});
            skCircle(sketch, "E83", {"center": v(-101, 90.7) * mm, "radius": 11.5 * mm});
            skCircle(sketch, "E84", {"center": v(-101, 90.7) * mm, "radius": 5 * mm});
            skSolve(sketch);
        }
        {
            var Q0;
            Q0=makeQuery(id+"F26.imprint","IMPRINT",FACE,{"disambiguationData":[TD([[makeQuery(id+"F26.imprint","IMPRINT",EDGE,{"derivedFrom":sQuery(id+"F26.wireOp",EDGE,"E82.4")}),-1.0]])]});
            extrude(context, id + "F27", {"entities" : qUnion([Q0]), "oppositeDirection" : true, "depth" : 6 * mm});
        }
        {
            var Q0;
            Q0=makeQuery(id+"F26.imprint","IMPRINT",FACE,{"disambiguationData":[TD([[makeQuery(id+"F26.imprint","IMPRINT",EDGE,{"derivedFrom":sQuery(id+"F26.wireOp",EDGE,"E82.0")}),1.0]])]});
            var Q1;
            Q1=makeQuery(id+"F26.imprint","IMPRINT",FACE,{"disambiguationData":[TD([[makeQuery(id+"F26.imprint","IMPRINT",EDGE,{"derivedFrom":sQuery(id+"F26.wireOp",EDGE,"E82.4")}),-1.0]])]});
            extrude(context, id + "F28", {"entities" : qUnion([Q0, Q1]), "operationType" : NewBodyOperationType.ADD, "depth" : 5 * mm});
        }
        {
            var Q0;
            Q0=makeQuery(id+"F1.opExtrude","SWEPT_FACE",FACE,{"disambiguationData":[OSD([sQuery(id+"F0.wireOp",EDGE,"E2")])]});
            var sketch = newSketch(context, id + "F29", { "sketchPlane" : qUnion([Q0])});
            skLineSegment(sketch, "E85.0", {"start": v(5, 102.2) * mm, "end": v(5, 79.2) * mm, "construction": true});
            skLineSegment(sketch, "E86", {"start": v(5, 90.7) * mm, "end": v(0, 90.7) * mm, "construction": true});
            skCircle(sketch, "E87", {"center": v(2.5, 90.7) * mm, "radius": 1.5 * mm});
            skCircle(sketch, "E88", {"center": v(2.5, 90.7) * mm, "radius": 0.75 * mm});
            skSolve(sketch);
        }
        {
            var Q0;
            Q0=makeQuery(id+"F29.imprint","IMPRINT",FACE,{"disambiguationData":[TD([[makeQuery(id+"F29.imprint","IMPRINT",EDGE,{"derivedFrom":sQuery(id+"F29.wireOp",EDGE,"E88")}),1.0]])]});
            extrude(context, id + "F30", {"entities" : qUnion([Q0]), "operationType" : NewBodyOperationType.REMOVE, "oppositeDirection" : true, "depth" : 22 * mm});
        }
        {
            var Q0;
            Q0=makeQuery(id+"F29.imprint","IMPRINT",FACE,{"disambiguationData":[TD([[makeQuery(id+"F29.imprint","IMPRINT",EDGE,{"derivedFrom":sQuery(id+"F29.wireOp",EDGE,"E87")}),1.0]])]});
            extrude(context, id + "F31", {"entities" : qUnion([Q0]), "operationType" : NewBodyOperationType.REMOVE, "oppositeDirection" : true, "depth" : 12.4 * mm});
        }
        {
            var Q0;
            Q0=makeQuery(id+"F1.opExtrude","CAP_FACE",FACE,{"disambiguationData":[OSD([sQuery(id+"F0.wireOp",EDGE,"E0"),sQuery(id+"F0.wireOp",EDGE,"E1"),sQuery(id+"F0.wireOp",EDGE,"E2"),sQuery(id+"F0.wireOp",EDGE,"E3"),sQuery(id+"F0.wireOp",EDGE,"E4"),sQuery(id+"F0.wireOp",EDGE,"E15"),sQuery(id+"F0.wireOp",EDGE,"E17"),sQuery(id+"F0.wireOp",EDGE,"E18"),sQuery(id+"F0.wireOp",EDGE,"E19"),sQuery(id+"F0.wireOp",EDGE,"E20"),sQuery(id+"F0.wireOp",EDGE,"E21"),sQuery(id+"F0.wireOp",EDGE,"E22"),sQuery(id+"F0.wireOp",EDGE,"E23"),sQuery(id+"F0.wireOp",EDGE,"E24"),sQuery(id+"F0.wireOp",EDGE,"E25.0.1.0"),sQuery(id+"F0.wireOp",EDGE,"E25.0.2.0"),sQuery(id+"F0.wireOp",EDGE,"E26.0.1.0"),sQuery(id+"F0.wireOp",EDGE,"E26.0.2.0"),sQuery(id+"F0.wireOp",EDGE,"E28"),sQuery(id+"F0.wireOp",EDGE,"E30"),sQuery(id+"F0.wireOp",EDGE,"E32"),sQuery(id+"F0.wireOp",EDGE,"E33.1.0"),sQuery(id+"F0.wireOp",EDGE,"E33.2.0"),sQuery(id+"F0.wireOp",EDGE,"E33.3.0"),sQuery(id+"F0.wireOp",EDGE,"E35"),sQuery(id+"F0.wireOp",EDGE,"E36.1.0"),sQuery(id+"F0.wireOp",EDGE,"E36.2.0"),sQuery(id+"F0.wireOp",EDGE,"E36.3.0"),sQuery(id+"F0.wireOp",EDGE,"E38"),sQuery(id+"F0.wireOp",EDGE,"E39.1.0"),sQuery(id+"F0.wireOp",EDGE,"E39.2.0"),sQuery(id+"F0.wireOp",EDGE,"E39.3.0"),sQuery(id+"F0.wireOp",EDGE,"E40"),sQuery(id+"F0.wireOp",EDGE,"E41"),sQuery(id+"F0.wireOp",EDGE,"E43"),sQuery(id+"F0.wireOp",EDGE,"E44.0.1.0"),sQuery(id+"F0.wireOp",EDGE,"E44.0.2.0"),sQuery(id+"F0.wireOp",EDGE,"E44.1.0.0"),sQuery(id+"F0.wireOp",EDGE,"E44.1.1.0"),sQuery(id+"F0.wireOp",EDGE,"E44.1.2.0"),sQuery(id+"F0.wireOp",EDGE,"E44.2.0.0"),sQuery(id+"F0.wireOp",EDGE,"E44.2.1.0"),sQuery(id+"F0.wireOp",EDGE,"E44.2.2.0"),sQuery(id+"F0.wireOp",EDGE,"E46"),sQuery(id+"F0.wireOp",EDGE,"E47.0.1.0"),sQuery(id+"F0.wireOp",EDGE,"E47.0.2.0"),sQuery(id+"F0.wireOp",EDGE,"E48.filletArc"),sQuery(id+"F0.wireOp",EDGE,"E49.1.0"),sQuery(id+"F0.wireOp",EDGE,"E49.2.0")])],"isStart":true});
            var sketch = newSketch(context, id + "F32", { "sketchPlane" : qUnion([Q0])});
            skCircle(sketch, "E89.0", {"center": v(-108, 24) * mm, "radius": 7 * mm});
            skCircle(sketch, "E89.1", {"center": v(-114.36, 30.36) * mm, "radius": 1.25 * mm});
            skCircle(sketch, "E89.2", {"center": v(-114.36, 17.64) * mm, "radius": 1.25 * mm});
            skCircle(sketch, "E89.3", {"center": v(-101.64, 17.64) * mm, "radius": 1.25 * mm});
            skCircle(sketch, "E89.4", {"center": v(-101.64, 30.36) * mm, "radius": 1.25 * mm});
            skCircle(sketch, "E90", {"center": v(-108, 24) * mm, "radius": 11.5 * mm});
            skCircle(sketch, "E91", {"center": v(-108, 24) * mm, "radius": 5.5 * mm});
            skSolve(sketch);
        }
        {
            var Q0;
            Q0=makeQuery(id+"F32.imprint","IMPRINT",FACE,{"disambiguationData":[TD([[makeQuery(id+"F32.imprint","IMPRINT",EDGE,{"derivedFrom":sQuery(id+"F32.wireOp",EDGE,"E89.0")}),-1.0]])]});
            extrude(context, id + "F33", {"entities" : qUnion([Q0]), "endBound" : BoundingType.SYMMETRIC, "oppositeDirection" : true, "depth" : 18 * mm});
        }
        {
            var Q0;
            Q0=makeQuery(id+"F32.imprint","IMPRINT",FACE,{"disambiguationData":[TD([[makeQuery(id+"F32.imprint","IMPRINT",EDGE,{"derivedFrom":sQuery(id+"F32.wireOp",EDGE,"E89.0")}),1.0]])]});
            var Q1;
            Q1=makeQuery(id+"F32.imprint","IMPRINT",FACE,{"disambiguationData":[TD([[makeQuery(id+"F32.imprint","IMPRINT",EDGE,{"derivedFrom":sQuery(id+"F32.wireOp",EDGE,"E89.0")}),-1.0]])]});
            extrude(context, id + "F34", {"entities" : qUnion([Q0, Q1]), "operationType" : NewBodyOperationType.ADD, "depth" : 5 * mm});
        }
        {
            var Q0;
            Q0=makeQuery(id+"F1.opExtrude","SWEPT_FACE",FACE,{"disambiguationData":[OSD([sQuery(id+"F0.wireOp",EDGE,"E2")])]});
            var sketch = newSketch(context, id + "F35", { "sketchPlane" : qUnion([Q0])});
            skLineSegment(sketch, "E92.0", {"start": v(5, 35.5) * mm, "end": v(5, 12.5) * mm, "construction": true});
            skLineSegment(sketch, "E93", {"start": v(5, 24) * mm, "end": v(0, 24) * mm, "construction": true});
            skCircle(sketch, "E94", {"center": v(2.5, 24) * mm, "radius": 1.5 * mm});
            skCircle(sketch, "E95", {"center": v(2.5, 24) * mm, "radius": 0.75 * mm});
            skSolve(sketch);
        }
        {
            var Q0;
            Q0=makeQuery(id+"F35.imprint","IMPRINT",FACE,{"disambiguationData":[TD([[makeQuery(id+"F35.imprint","IMPRINT",EDGE,{"derivedFrom":sQuery(id+"F35.wireOp",EDGE,"E95")}),1.0]])]});
            extrude(context, id + "F36", {"entities" : qUnion([Q0]), "operationType" : NewBodyOperationType.REMOVE, "oppositeDirection" : true, "depth" : 10 * mm});
        }
        {
            var Q0;
            Q0=makeQuery(id+"F35.imprint","IMPRINT",FACE,{"disambiguationData":[TD([[makeQuery(id+"F35.imprint","IMPRINT",EDGE,{"derivedFrom":sQuery(id+"F35.wireOp",EDGE,"E94")}),1.0]])]});
            extrude(context, id + "F37", {"entities" : qUnion([Q0]), "operationType" : NewBodyOperationType.REMOVE, "oppositeDirection" : true, "depth" : 5.4 * mm});
        }
        {
            var Q0;
            Q0=makeQuery(id+"F16.opExtrude","CAP_EDGE",EDGE,{"disambiguationData":[OSD([sQuery(id+"F14.wireOp",EDGE,"E71")])],"isStart":false});
            var Q1;
            Q1=makeQuery(id+"F23.opExtrude","CAP_EDGE",EDGE,{"disambiguationData":[OSD([sQuery(id+"F21.wireOp",EDGE,"E77")])],"isStart":false});
            var Q2;
            Q2=makeQuery(id+"F28.opExtrude","CAP_EDGE",EDGE,{"disambiguationData":[OSD([sQuery(id+"F26.wireOp",EDGE,"E83")])],"isStart":false});
            var Q3;
            Q3=makeQuery(id+"F34.opExtrude","CAP_EDGE",EDGE,{"disambiguationData":[OSD([sQuery(id+"F32.wireOp",EDGE,"E90")])],"isStart":false});
            fillet(context, id + "F38", {"entities" : qUnion([Q0, Q1, Q2, Q3]), "radius" : 1 * mm, "tangentPropagation" : true, "allowEdgeOverflow" : false});
        }
        {
            var Q0;
            Q0=makeQuery(id+"F1.opExtrude","CAP_FACE",FACE,{"disambiguationData":[OSD([sQuery(id+"F0.wireOp",EDGE,"E0"),sQuery(id+"F0.wireOp",EDGE,"E1"),sQuery(id+"F0.wireOp",EDGE,"E2"),sQuery(id+"F0.wireOp",EDGE,"E3"),sQuery(id+"F0.wireOp",EDGE,"E4"),sQuery(id+"F0.wireOp",EDGE,"E15"),sQuery(id+"F0.wireOp",EDGE,"E17"),sQuery(id+"F0.wireOp",EDGE,"E18"),sQuery(id+"F0.wireOp",EDGE,"E19"),sQuery(id+"F0.wireOp",EDGE,"E20"),sQuery(id+"F0.wireOp",EDGE,"E21"),sQuery(id+"F0.wireOp",EDGE,"E22"),sQuery(id+"F0.wireOp",EDGE,"E23"),sQuery(id+"F0.wireOp",EDGE,"E24"),sQuery(id+"F0.wireOp",EDGE,"E25.0.1.0"),sQuery(id+"F0.wireOp",EDGE,"E25.0.2.0"),sQuery(id+"F0.wireOp",EDGE,"E26.0.1.0"),sQuery(id+"F0.wireOp",EDGE,"E26.0.2.0"),sQuery(id+"F0.wireOp",EDGE,"E28"),sQuery(id+"F0.wireOp",EDGE,"E30"),sQuery(id+"F0.wireOp",EDGE,"E32"),sQuery(id+"F0.wireOp",EDGE,"E33.1.0"),sQuery(id+"F0.wireOp",EDGE,"E33.2.0"),sQuery(id+"F0.wireOp",EDGE,"E33.3.0"),sQuery(id+"F0.wireOp",EDGE,"E35"),sQuery(id+"F0.wireOp",EDGE,"E36.1.0"),sQuery(id+"F0.wireOp",EDGE,"E36.2.0"),sQuery(id+"F0.wireOp",EDGE,"E36.3.0"),sQuery(id+"F0.wireOp",EDGE,"E38"),sQuery(id+"F0.wireOp",EDGE,"E39.1.0"),sQuery(id+"F0.wireOp",EDGE,"E39.2.0"),sQuery(id+"F0.wireOp",EDGE,"E39.3.0"),sQuery(id+"F0.wireOp",EDGE,"E40"),sQuery(id+"F0.wireOp",EDGE,"E41"),sQuery(id+"F0.wireOp",EDGE,"E43"),sQuery(id+"F0.wireOp",EDGE,"E44.0.1.0"),sQuery(id+"F0.wireOp",EDGE,"E44.0.2.0"),sQuery(id+"F0.wireOp",EDGE,"E44.1.0.0"),sQuery(id+"F0.wireOp",EDGE,"E44.1.1.0"),sQuery(id+"F0.wireOp",EDGE,"E44.1.2.0"),sQuery(id+"F0.wireOp",EDGE,"E44.2.0.0"),sQuery(id+"F0.wireOp",EDGE,"E44.2.1.0"),sQuery(id+"F0.wireOp",EDGE,"E44.2.2.0"),sQuery(id+"F0.wireOp",EDGE,"E46"),sQuery(id+"F0.wireOp",EDGE,"E47.0.1.0"),sQuery(id+"F0.wireOp",EDGE,"E47.0.2.0"),sQuery(id+"F0.wireOp",EDGE,"E48.filletArc"),sQuery(id+"F0.wireOp",EDGE,"E49.1.0"),sQuery(id+"F0.wireOp",EDGE,"E49.2.0")])],"isStart":false});
            var sketch = newSketch(context, id + "F39", { "sketchPlane" : qUnion([Q0])});
            skCircle(sketch, "E96.0", {"center": v(3, 28.5) * mm, "radius": 1.25 * mm});
            skCircle(sketch, "E96.1", {"center": v(3, 21.5) * mm, "radius": 1.25 * mm});
            skCircle(sketch, "E96.2", {"center": v(3, 14.5) * mm, "radius": 1.25 * mm});
            skLineSegment(sketch, "E97", {"start": v(6, 31.5) * mm, "end": v(0, 31.5) * mm});
            skLineSegment(sketch, "E98", {"start": v(6, 31.5) * mm, "end": v(6, 11.5) * mm});
            skLineSegment(sketch, "E99", {"start": v(6, 11.5) * mm, "end": v(-14, 11.5) * mm});
            skLineSegment(sketch, "E100", {"start": v(-14, 11.5) * mm, "end": v(-14, 19.5) * mm, "construction": true});
            skCircle(sketch, "E101", {"center": v(-14, 19.5) * mm, "radius": 8 * mm});
            skLineSegment(sketch, "E102", {"start": v(0, 31.5) * mm, "end": v(-16.06, 27.23) * mm});
            skCircle(sketch, "E103", {"center": v(-14, 19.5) * mm, "radius": 6 * mm});
            skCircle(sketch, "E104", {"center": v(-14, 19.5) * mm, "radius": 5 * mm});
            skCircle(sketch, "E105", {"center": v(-14, 19.5) * mm, "radius": 3.5 * mm});
            skSolve(sketch);
        }
        {
            var Q0;
            Q0=makeQuery(id+"F39.imprint","IMPRINT",FACE,{"disambiguationData":[TD([[makeQuery(id+"F39.imprint","IMPRINT",EDGE,{"derivedFrom":sQuery(id+"F39.wireOp",EDGE,"E96.0")}),-1.0]])]});
            var Q1;
            {var subQ3=sQuery(id+"F39.wireOp",EDGE,"E102");Q1=makeQuery(id+"F39.imprint","IMPRINT",FACE,{"disambiguationData":[TD([[makeQuery(id+"F39.imprint","IMPRINT",EDGE,{"derivedFrom":subQ3}),1.0]])]});}
            var Q2;
            Q2=makeQuery(id+"F39.imprint","IMPRINT",FACE,{"disambiguationData":[TD([[makeQuery(id+"F39.imprint","IMPRINT",EDGE,{"derivedFrom":sQuery(id+"F39.wireOp",EDGE,"E103")}),-1.0]])]});
            var Q3;
            Q3=makeQuery(id+"F39.imprint","IMPRINT",FACE,{"disambiguationData":[TD([[makeQuery(id+"F39.imprint","IMPRINT",EDGE,{"derivedFrom":sQuery(id+"F39.wireOp",EDGE,"E103")}),1.0]])]});
            extrude(context, id + "F40", {"entities" : qUnion([Q0, Q1, Q2, Q3]), "depth" : 1.5 * mm});
        }
        {
            var Q0;
            Q0=makeQuery(id+"F39.imprint","IMPRINT",FACE,{"disambiguationData":[TD([[makeQuery(id+"F39.imprint","IMPRINT",EDGE,{"derivedFrom":sQuery(id+"F39.wireOp",EDGE,"E104")}),1.0]])]});
            extrude(context, id + "F41", {"entities" : qUnion([Q0]), "depth" : 4 * mm});
        }
        {
            var Q0;
            Q0=makeQuery(id+"F39.imprint","IMPRINT",FACE,{"disambiguationData":[TD([[makeQuery(id+"F39.imprint","IMPRINT",EDGE,{"derivedFrom":sQuery(id+"F39.wireOp",EDGE,"E103")}),1.0]])]});
            var Q1;
            Q1=makeQuery(id+"F39.imprint","IMPRINT",FACE,{"disambiguationData":[TD([[makeQuery(id+"F39.imprint","IMPRINT",EDGE,{"derivedFrom":sQuery(id+"F39.wireOp",EDGE,"E104")}),1.0]])]});
            extrude(context, id + "F42", {"entities" : qUnion([Q0, Q1]), "operationType" : NewBodyOperationType.ADD, "oppositeDirection" : true, "depth" : 2.5 * mm});
        }
        {
            var Q0;
            Q0=makeQuery(id+"F1.opExtrude","CAP_FACE",FACE,{"disambiguationData":[OSD([sQuery(id+"F0.wireOp",EDGE,"E0"),sQuery(id+"F0.wireOp",EDGE,"E1"),sQuery(id+"F0.wireOp",EDGE,"E2"),sQuery(id+"F0.wireOp",EDGE,"E3"),sQuery(id+"F0.wireOp",EDGE,"E4"),sQuery(id+"F0.wireOp",EDGE,"E15"),sQuery(id+"F0.wireOp",EDGE,"E17"),sQuery(id+"F0.wireOp",EDGE,"E18"),sQuery(id+"F0.wireOp",EDGE,"E19"),sQuery(id+"F0.wireOp",EDGE,"E20"),sQuery(id+"F0.wireOp",EDGE,"E21"),sQuery(id+"F0.wireOp",EDGE,"E22"),sQuery(id+"F0.wireOp",EDGE,"E23"),sQuery(id+"F0.wireOp",EDGE,"E24"),sQuery(id+"F0.wireOp",EDGE,"E25.0.1.0"),sQuery(id+"F0.wireOp",EDGE,"E25.0.2.0"),sQuery(id+"F0.wireOp",EDGE,"E26.0.1.0"),sQuery(id+"F0.wireOp",EDGE,"E26.0.2.0"),sQuery(id+"F0.wireOp",EDGE,"E28"),sQuery(id+"F0.wireOp",EDGE,"E30"),sQuery(id+"F0.wireOp",EDGE,"E32"),sQuery(id+"F0.wireOp",EDGE,"E33.1.0"),sQuery(id+"F0.wireOp",EDGE,"E33.2.0"),sQuery(id+"F0.wireOp",EDGE,"E33.3.0"),sQuery(id+"F0.wireOp",EDGE,"E35"),sQuery(id+"F0.wireOp",EDGE,"E36.1.0"),sQuery(id+"F0.wireOp",EDGE,"E36.2.0"),sQuery(id+"F0.wireOp",EDGE,"E36.3.0"),sQuery(id+"F0.wireOp",EDGE,"E38"),sQuery(id+"F0.wireOp",EDGE,"E39.1.0"),sQuery(id+"F0.wireOp",EDGE,"E39.2.0"),sQuery(id+"F0.wireOp",EDGE,"E39.3.0"),sQuery(id+"F0.wireOp",EDGE,"E40"),sQuery(id+"F0.wireOp",EDGE,"E41"),sQuery(id+"F0.wireOp",EDGE,"E43"),sQuery(id+"F0.wireOp",EDGE,"E44.0.1.0"),sQuery(id+"F0.wireOp",EDGE,"E44.0.2.0"),sQuery(id+"F0.wireOp",EDGE,"E44.1.0.0"),sQuery(id+"F0.wireOp",EDGE,"E44.1.1.0"),sQuery(id+"F0.wireOp",EDGE,"E44.1.2.0"),sQuery(id+"F0.wireOp",EDGE,"E44.2.0.0"),sQuery(id+"F0.wireOp",EDGE,"E44.2.1.0"),sQuery(id+"F0.wireOp",EDGE,"E44.2.2.0"),sQuery(id+"F0.wireOp",EDGE,"E46"),sQuery(id+"F0.wireOp",EDGE,"E47.0.1.0"),sQuery(id+"F0.wireOp",EDGE,"E47.0.2.0"),sQuery(id+"F0.wireOp",EDGE,"E48.filletArc"),sQuery(id+"F0.wireOp",EDGE,"E49.1.0"),sQuery(id+"F0.wireOp",EDGE,"E49.2.0")])],"isStart":false});
            cPlane(context, id + "F43", {"entities" : qUnion([Q0]), "cplaneType" : CPlaneType.OFFSET, "offset" : 50 * mm, "width" : 150 * mm, "height" : 150 * mm});
        }
        {
            var Q0;
            Q0=qCreatedBy(id+"F43.planeOp",FACE);
            var sketch = newSketch(context, id + "F44", { "sketchPlane" : qUnion([Q0])});
            skCircle(sketch, "E106.0", {"center": v(3, 28.5) * mm, "radius": 1.25 * mm});
            skCircle(sketch, "E106.1", {"center": v(3, 21.5) * mm, "radius": 1.25 * mm});
            skCircle(sketch, "E106.2", {"center": v(3, 14.5) * mm, "radius": 1.25 * mm});
            skCircle(sketch, "E106.3", {"center": v(-14, 19.5) * mm, "radius": 3.5 * mm});
            skCircle(sketch, "E106.4", {"center": v(-14, 19.5) * mm, "radius": 5 * mm});
            skCircle(sketch, "E106.5", {"center": v(-14, 19.5) * mm, "radius": 6 * mm});
            skCircle(sketch, "E107.0", {"center": v(-14, 19.5) * mm, "radius": 8 * mm});
            skLineSegment(sketch, "E108", {"start": v(-14, 11.5) * mm, "end": v(6, 11.5) * mm});
            skLineSegment(sketch, "E109", {"start": v(6, 11.5) * mm, "end": v(6, 31.5) * mm});
            skLineSegment(sketch, "E110", {"start": v(6, 31.5) * mm, "end": v(-11, 41.5) * mm});
            skLineSegment(sketch, "E111", {"start": v(-11, 41.5) * mm, "end": v(-18, 36.5) * mm});
            skLineSegment(sketch, "E112", {"start": v(-18, 36.5) * mm, "end": v(-21.76, 21.44) * mm});
            skLineSegment(sketch, "E113", {"start": v(-14, 19.5) * mm, "end": v(-14, 35) * mm, "construction": true});
            skLineSegment(sketch, "E114", {"start": v(-14, 35) * mm, "end": v(-13, 35) * mm, "construction": true});
            skCircle(sketch, "E115", {"center": v(-13, 35) * mm, "radius": 1.25 * mm});
            skSolve(sketch);
        }
        {
            var Q0;
            Q0=makeQuery(id+"F44.imprint","IMPRINT",FACE,{"disambiguationData":[TD([[makeQuery(id+"F44.imprint","IMPRINT",EDGE,{"derivedFrom":sQuery(id+"F44.wireOp",EDGE,"E106.0")}),-1.0]])]});
            var Q1;
            Q1=makeQuery(id+"F44.imprint","IMPRINT",FACE,{"disambiguationData":[TD([[makeQuery(id+"F44.imprint","IMPRINT",EDGE,{"derivedFrom":sQuery(id+"F44.wireOp",EDGE,"E106.5")}),-1.0]])]});
            var Q2;
            Q2=makeQuery(id+"F44.imprint","IMPRINT",FACE,{"disambiguationData":[TD([[makeQuery(id+"F44.imprint","IMPRINT",EDGE,{"derivedFrom":sQuery(id+"F44.wireOp",EDGE,"E106.4")}),-1.0]])]});
            extrude(context, id + "F45", {"entities" : qUnion([Q0, Q1, Q2]), "depth" : 1.5 * mm});
        }
        {
            var Q0;
            Q0=makeQuery(id+"F45.opExtrude","CAP_FACE",FACE,{"disambiguationData":[OSD([sQuery(id+"F44.wireOp",EDGE,"E106.0"),sQuery(id+"F44.wireOp",EDGE,"E106.1"),sQuery(id+"F44.wireOp",EDGE,"E106.2"),sQuery(id+"F44.wireOp",EDGE,"E106.4"),sQuery(id+"F44.wireOp",EDGE,"E107.0"),sQuery(id+"F44.wireOp",EDGE,"E108"),sQuery(id+"F44.wireOp",EDGE,"E109"),sQuery(id+"F44.wireOp",EDGE,"E110"),sQuery(id+"F44.wireOp",EDGE,"E111"),sQuery(id+"F44.wireOp",EDGE,"E112"),sQuery(id+"F44.wireOp",EDGE,"E115")])],"isStart":false});
            var sketch = newSketch(context, id + "F46", { "sketchPlane" : qUnion([Q0])});
            skCircle(sketch, "E116.0", {"center": v(-13, 35) * mm, "radius": 1.25 * mm});
            skLineSegment(sketch, "E117.rect.bottom", {"start": v(-17, 30) * mm, "end": v(-9, 30) * mm});
            skLineSegment(sketch, "E117.rect.top", {"start": v(-17, 40) * mm, "end": v(-9, 40) * mm});
            skLineSegment(sketch, "E117.rect.left", {"start": v(-17, 30) * mm, "end": v(-17, 40) * mm});
            skLineSegment(sketch, "E117.rect.right", {"start": v(-9, 30) * mm, "end": v(-9, 40) * mm});
            skSolve(sketch);
        }
        {
            var Q0;
            Q0=makeQuery(id+"F46.imprint","IMPRINT",FACE,{"disambiguationData":[TD([[makeQuery(id+"F46.imprint","IMPRINT",EDGE,{"derivedFrom":sQuery(id+"F46.wireOp",EDGE,"E116.0")}),-1.0]])]});
            var Q1;
            {var subQ1=sQuery(id+"F46.wireOp",EDGE,"E117.rect.left");var subQ3=sQuery(id+"F46.wireOp",EDGE,"E117.rect.top");var subQ5=makeQuery(id+"F46.imprint","INTERSECT",VERTEX,{"derivedFrom":[subQ3,subQ1]});Q1=makeQuery(id+"F46.imprint","IMPRINT",FACE,{"disambiguationData":[TD([[makeQuery(id+"F46.imprint","IMPRINT",EDGE,{"disambiguationData":[TD([[subQ5,-1.0]])],"derivedFrom":subQ3}),-1.0]])]});}
            var Q2;
            Q2=makeQuery(id+"F46.imprint","IMPRINT",FACE,{"disambiguationData":[TD([[makeQuery(id+"F46.imprint","IMPRINT",EDGE,{"derivedFrom":sQuery(id+"F46.wireOp",EDGE,"E116.0")}),1.0]])]});
            extrude(context, id + "F47", {"entities" : qUnion([Q0, Q1, Q2]), "depth" : 9.5 * mm});
        }
        {
            var Q0;
            Q0=makeQuery(id+"F47.opExtrude","SWEPT_FACE",FACE,{"disambiguationData":[OSD([sQuery(id+"F46.wireOp",EDGE,"E117.rect.top")])]});
            var sketch = newSketch(context, id + "F48", { "sketchPlane" : qUnion([Q0])});
            skLineSegment(sketch, "E118", {"start": v(53, -13) * mm, "end": v(58.5, -13) * mm, "construction": true});
            skCircle(sketch, "E119", {"center": v(58.5, -13) * mm, "radius": 2 * mm});
            skSolve(sketch);
        }
        {
            var Q0;
            Q0=makeQuery(id+"F48.imprint","IMPRINT",FACE,{"disambiguationData":[TD([[makeQuery(id+"F48.imprint","IMPRINT",EDGE,{"derivedFrom":sQuery(id+"F48.wireOp",EDGE,"E119")}),1.0]])]});
            extrude(context, id + "F49", {"entities" : qUnion([Q0]), "operationType" : NewBodyOperationType.REMOVE, "oppositeDirection" : true, "depth" : 10 * mm});
        }
        {
            var Q0;
            Q0=makeQuery(id+"F47.opExtrude","CAP_EDGE",EDGE,{"disambiguationData":[OSD([sQuery(id+"F46.wireOp",EDGE,"E117.rect.left")])],"isStart":false});
            var Q1;
            Q1=makeQuery(id+"F47.opExtrude","CAP_EDGE",EDGE,{"disambiguationData":[OSD([sQuery(id+"F46.wireOp",EDGE,"E117.rect.right")])],"isStart":false});
            fillet(context, id + "F50", {"entities" : qUnion([Q0, Q1]), "radius" : 4 * mm, "tangentPropagation" : true, "allowEdgeOverflow" : false});
        }
        {
            var Q0;
            Q0=makeQuery(id+"F46.imprint","IMPRINT",FACE,{"disambiguationData":[TD([[makeQuery(id+"F46.imprint","IMPRINT",EDGE,{"derivedFrom":sQuery(id+"F46.wireOp",EDGE,"E116.0")}),1.0]])]});
            extrude(context, id + "F51", {"entities" : qUnion([Q0]), "operationType" : NewBodyOperationType.REMOVE, "depth" : 5.5 * mm});
        }
        {
            var Q0;
            Q0=qCreatedBy(id+"F43.planeOp",FACE);
            var sketch = newSketch(context, id + "F52", { "sketchPlane" : qUnion([Q0])});
            skCircle(sketch, "E120.0", {"center": v(109, 127.5) * mm, "radius": 1.5 * mm});
            skLineSegment(sketch, "E121.rect.bottom", {"start": v(106, 124.5) * mm, "end": v(112, 124.5) * mm});
            skLineSegment(sketch, "E121.rect.top", {"start": v(106, 130.5) * mm, "end": v(112, 130.5) * mm});
            skLineSegment(sketch, "E121.rect.left", {"start": v(106, 124.5) * mm, "end": v(106, 130.5) * mm});
            skLineSegment(sketch, "E121.rect.right", {"start": v(112, 124.5) * mm, "end": v(112, 130.5) * mm});
            skSolve(sketch);
        }
        {
            var Q0;
            Q0=makeQuery(id+"F52.imprint","IMPRINT",FACE,{"disambiguationData":[TD([[makeQuery(id+"F52.imprint","IMPRINT",EDGE,{"derivedFrom":sQuery(id+"F52.wireOp",EDGE,"E120.0")}),1.0]])]});
            extrude(context, id + "F53", {"entities" : qUnion([Q0]), "oppositeDirection" : true, "depth" : 4 * mm});
        }
        {
            var Q0;
            Q0=makeQuery(id+"F52.imprint","IMPRINT",FACE,{"disambiguationData":[TD([[makeQuery(id+"F52.imprint","IMPRINT",EDGE,{"derivedFrom":sQuery(id+"F52.wireOp",EDGE,"E120.0")}),-1.0]])]});
            var Q1;
            Q1=makeQuery(id+"F52.imprint","IMPRINT",FACE,{"disambiguationData":[TD([[makeQuery(id+"F52.imprint","IMPRINT",EDGE,{"derivedFrom":sQuery(id+"F52.wireOp",EDGE,"E120.0")}),1.0]])]});
            extrude(context, id + "F54", {"entities" : qUnion([Q0, Q1]), "operationType" : NewBodyOperationType.ADD, "depth" : 10 * mm});
        }
        {
            var Q0;
            Q0=makeQuery(id+"F54.opExtrude","SWEPT_FACE",FACE,{"disambiguationData":[OSD([sQuery(id+"F52.wireOp",EDGE,"E121.rect.top")])]});
            var sketch = newSketch(context, id + "F55", { "sketchPlane" : qUnion([Q0])});
            skLineSegment(sketch, "E122", {"start": v(51.5, 109) * mm, "end": v(58.5, 109) * mm, "construction": true});
            skCircle(sketch, "E123", {"center": v(58.5, 109) * mm, "radius": 2 * mm});
            skSolve(sketch);
        }
        {
            var Q0;
            Q0=makeQuery(id+"F55.imprint","IMPRINT",FACE,{"disambiguationData":[TD([[makeQuery(id+"F55.imprint","IMPRINT",EDGE,{"derivedFrom":sQuery(id+"F55.wireOp",EDGE,"E123")}),1.0]])]});
            extrude(context, id + "F56", {"entities" : qUnion([Q0]), "operationType" : NewBodyOperationType.REMOVE, "oppositeDirection" : true, "depth" : 6 * mm});
        }
        {
            var Q0;
            Q0=makeQuery(id+"F54.opExtrude","CAP_EDGE",EDGE,{"disambiguationData":[OSD([sQuery(id+"F52.wireOp",EDGE,"E121.rect.left")])],"isStart":false});
            var Q1;
            Q1=makeQuery(id+"F54.opExtrude","CAP_EDGE",EDGE,{"disambiguationData":[OSD([sQuery(id+"F52.wireOp",EDGE,"E121.rect.right")])],"isStart":false});
            fillet(context, id + "F57", {"entities" : qUnion([Q0, Q1]), "radius" : 3 * mm, "tangentPropagation" : true, "allowEdgeOverflow" : false});
        }
        {
            var Q0;
            Q0=makeQuery(id+"F1.opExtrude","CAP_FACE",FACE,{"disambiguationData":[OSD([sQuery(id+"F0.wireOp",EDGE,"E0"),sQuery(id+"F0.wireOp",EDGE,"E1"),sQuery(id+"F0.wireOp",EDGE,"E2"),sQuery(id+"F0.wireOp",EDGE,"E3"),sQuery(id+"F0.wireOp",EDGE,"E4"),sQuery(id+"F0.wireOp",EDGE,"E15"),sQuery(id+"F0.wireOp",EDGE,"E17"),sQuery(id+"F0.wireOp",EDGE,"E18"),sQuery(id+"F0.wireOp",EDGE,"E19"),sQuery(id+"F0.wireOp",EDGE,"E20"),sQuery(id+"F0.wireOp",EDGE,"E21"),sQuery(id+"F0.wireOp",EDGE,"E22"),sQuery(id+"F0.wireOp",EDGE,"E23"),sQuery(id+"F0.wireOp",EDGE,"E24"),sQuery(id+"F0.wireOp",EDGE,"E25.0.1.0"),sQuery(id+"F0.wireOp",EDGE,"E25.0.2.0"),sQuery(id+"F0.wireOp",EDGE,"E26.0.1.0"),sQuery(id+"F0.wireOp",EDGE,"E26.0.2.0"),sQuery(id+"F0.wireOp",EDGE,"E28"),sQuery(id+"F0.wireOp",EDGE,"E30"),sQuery(id+"F0.wireOp",EDGE,"E32"),sQuery(id+"F0.wireOp",EDGE,"E33.1.0"),sQuery(id+"F0.wireOp",EDGE,"E33.2.0"),sQuery(id+"F0.wireOp",EDGE,"E33.3.0"),sQuery(id+"F0.wireOp",EDGE,"E35"),sQuery(id+"F0.wireOp",EDGE,"E36.1.0"),sQuery(id+"F0.wireOp",EDGE,"E36.2.0"),sQuery(id+"F0.wireOp",EDGE,"E36.3.0"),sQuery(id+"F0.wireOp",EDGE,"E38"),sQuery(id+"F0.wireOp",EDGE,"E39.1.0"),sQuery(id+"F0.wireOp",EDGE,"E39.2.0"),sQuery(id+"F0.wireOp",EDGE,"E39.3.0"),sQuery(id+"F0.wireOp",EDGE,"E40"),sQuery(id+"F0.wireOp",EDGE,"E41"),sQuery(id+"F0.wireOp",EDGE,"E43"),sQuery(id+"F0.wireOp",EDGE,"E44.0.1.0"),sQuery(id+"F0.wireOp",EDGE,"E44.0.2.0"),sQuery(id+"F0.wireOp",EDGE,"E44.1.0.0"),sQuery(id+"F0.wireOp",EDGE,"E44.1.1.0"),sQuery(id+"F0.wireOp",EDGE,"E44.1.2.0"),sQuery(id+"F0.wireOp",EDGE,"E44.2.0.0"),sQuery(id+"F0.wireOp",EDGE,"E44.2.1.0"),sQuery(id+"F0.wireOp",EDGE,"E44.2.2.0"),sQuery(id+"F0.wireOp",EDGE,"E46"),sQuery(id+"F0.wireOp",EDGE,"E47.0.1.0"),sQuery(id+"F0.wireOp",EDGE,"E47.0.2.0"),sQuery(id+"F0.wireOp",EDGE,"E48.filletArc"),sQuery(id+"F0.wireOp",EDGE,"E49.1.0"),sQuery(id+"F0.wireOp",EDGE,"E49.2.0")])],"isStart":true});
            var sketch = newSketch(context, id + "F58", { "sketchPlane" : qUnion([Q0])});
            skCircle(sketch, "E124.0", {"center": v(-116, 102) * mm, "radius": 1.25 * mm});
            skCircle(sketch, "E125", {"center": v(-116, 102) * mm, "radius": 3 * mm});
            skSolve(sketch);
        }
        {
            var Q0;
            Q0=makeQuery(id+"F58.imprint","IMPRINT",FACE,{"disambiguationData":[TD([[makeQuery(id+"F58.imprint","IMPRINT",EDGE,{"derivedFrom":sQuery(id+"F58.wireOp",EDGE,"E124.0")}),-1.0]])]});
            extrude(context, id + "F59", {"entities" : qUnion([Q0]), "oppositeDirection" : true, "depth" : 5 * mm});
        }
        {
            var Q0;
            Q0=makeQuery(id+"F58.imprint","IMPRINT",FACE,{"disambiguationData":[TD([[makeQuery(id+"F58.imprint","IMPRINT",EDGE,{"derivedFrom":sQuery(id+"F58.wireOp",EDGE,"E124.0")}),-1.0]])]});
            extrude(context, id + "F60", {"entities" : qUnion([Q0]), "operationType" : NewBodyOperationType.ADD, "depth" : 13 * mm});
        }
        {
            var Q0;
            Q0=makeQuery(id+"F58.imprint","IMPRINT",FACE,{"disambiguationData":[TD([[makeQuery(id+"F58.imprint","IMPRINT",EDGE,{"derivedFrom":sQuery(id+"F58.wireOp",EDGE,"E124.0")}),1.0]])]});
            extrude(context, id + "F61", {"entities" : qUnion([Q0]), "operationType" : NewBodyOperationType.ADD, "depth" : 8 * mm});
        }
        {
            var Q0;
            Q0=makeQuery(id+"F61.opExtrude","CAP_FACE",FACE,{"disambiguationData":[OSD([sQuery(id+"F58.wireOp",EDGE,"E124.0"),sQuery(id+"F58.wireOp",EDGE,"E125")])],"isStart":false});
            var sketch = newSketch(context, id + "F62", { "sketchPlane" : qUnion([Q0])});
            skCircle(sketch, "E126.0", {"center": v(-116, 102) * mm, "radius": 3 * mm});
            skCircle(sketch, "E126.1", {"center": v(-116, 102) * mm, "radius": 1.25 * mm});
            skLineSegment(sketch, "E127.bottom", {"start": v(-116, 103.5) * mm, "end": v(-127.5, 103.5) * mm});
            skLineSegment(sketch, "E127.top", {"start": v(-116, 100.5) * mm, "end": v(-127.5, 100.5) * mm});
            skLineSegment(sketch, "E127.left", {"start": v(-116, 103.5) * mm, "end": v(-116, 100.5) * mm});
            skLineSegment(sketch, "E127.right", {"start": v(-127.5, 103.5) * mm, "end": v(-127.5, 100.5) * mm});
            skArc(sketch, "E128", {"start": v(-127.5, 103.5) * mm, "mid": v(-129, 102) * mm, "end": v(-127.5, 100.5) * mm});
            skSolve(sketch);
        }
        {
            var Q0;
            {var subQ3=sQuery(id+"F62.wireOp",EDGE,"E127.right");Q0=makeQuery(id+"F62.imprint","IMPRINT",FACE,{"disambiguationData":[TD([[makeQuery(id+"F62.imprint","IMPRINT",EDGE,{"derivedFrom":subQ3}),1.0]])]});}
            var Q1;
            Q1=makeQuery(id+"F62.imprint","IMPRINT",FACE,{"disambiguationData":[TD([[makeQuery(id+"F62.imprint","IMPRINT",EDGE,{"derivedFrom":sQuery(id+"F62.wireOp",EDGE,"E127.right")}),-1.0]])]});
            var Q2;
            {var subQ6=sQuery(id+"F62.wireOp",EDGE,"E127.bottom");var subQ8=sQuery(id+"F62.wireOp",EDGE,"E126.0");var subQ10=makeQuery(id+"F62.imprint","INTERSECT",VERTEX,{"derivedFrom":[subQ8,subQ6]});Q2=makeQuery(id+"F62.imprint","IMPRINT",FACE,{"disambiguationData":[TD([[makeQuery(id+"F62.imprint","IMPRINT",EDGE,{"disambiguationData":[TD([[subQ10,-1.0]])],"derivedFrom":subQ8}),1.0]])]});}
            var Q3;
            {var subQ6=sQuery(id+"F62.wireOp",EDGE,"E127.bottom");var subQ8=sQuery(id+"F62.wireOp",EDGE,"E126.0");var subQ10=makeQuery(id+"F62.imprint","INTERSECT",VERTEX,{"derivedFrom":[subQ8,subQ6]});Q3=makeQuery(id+"F62.imprint","IMPRINT",FACE,{"disambiguationData":[TD([[makeQuery(id+"F62.imprint","IMPRINT",EDGE,{"disambiguationData":[TD([[subQ10,1.0]])],"derivedFrom":subQ8}),1.0]])]});}
            extrude(context, id + "F63", {"entities" : qUnion([Q0, Q1, Q2, Q3]), "depth" : 1.5 * mm});
        }
        {
            var Q0;
            Q0=makeQuery(id+"F1.opExtrude","SWEPT_FACE",FACE,{"disambiguationData":[OSD([sQuery(id+"F0.wireOp",EDGE,"E2")])]});
            var sketch = newSketch(context, id + "F64", { "sketchPlane" : qUnion([Q0])});
            skCircle(sketch, "E129.0", {"center": v(2.5, 90.7) * mm, "radius": 1.5 * mm});
            skCircle(sketch, "E130", {"center": v(2.5, 90.7) * mm, "radius": 2.25 * mm});
            skCircle(sketch, "E131", {"center": v(2.5, 90.7) * mm, "radius": 1 * mm});
            skCircle(sketch, "E132.cCircle", {"center": v(2.5, 90.7) * mm, "radius": 1.25 * mm, "construction": true});
            skLineSegment(sketch, "E132.0", {"start": v(1.25, 89.98) * mm, "end": v(1.25, 91.42) * mm});
            skLineSegment(sketch, "E132.1", {"start": v(1.25, 91.42) * mm, "end": v(2.5, 92.14) * mm});
            skLineSegment(sketch, "E132.2", {"start": v(2.5, 92.14) * mm, "end": v(3.75, 91.42) * mm});
            skLineSegment(sketch, "E132.3", {"start": v(3.75, 91.42) * mm, "end": v(3.75, 89.98) * mm});
            skLineSegment(sketch, "E132.4", {"start": v(3.75, 89.98) * mm, "end": v(2.5, 89.26) * mm});
            skLineSegment(sketch, "E132.5", {"start": v(2.5, 89.26) * mm, "end": v(1.25, 89.98) * mm});
            skPoint(sketch, "E132.0.midPoint", {"position": v(1.25, 90.7) * mm});
            skSolve(sketch);
        }
        {
            var Q0;
            Q0=makeQuery(id+"F64.imprint","IMPRINT",FACE,{"disambiguationData":[TD([[makeQuery(id+"F64.imprint","IMPRINT",EDGE,{"derivedFrom":sQuery(id+"F64.wireOp",EDGE,"E131")}),-1.0]])]});
            var Q1;
            Q1=makeQuery(id+"F64.imprint","IMPRINT",FACE,{"disambiguationData":[TD([[makeQuery(id+"F64.imprint","IMPRINT",EDGE,{"derivedFrom":sQuery(id+"F64.wireOp",EDGE,"E129.0")}),1.0]])]});
            extrude(context, id + "F65", {"entities" : qUnion([Q0, Q1]), "oppositeDirection" : true, "depth" : 5 * mm});
        }
        {
            var Q0;
            Q0=makeQuery(id+"F64.imprint","IMPRINT",FACE,{"disambiguationData":[TD([[makeQuery(id+"F64.imprint","IMPRINT",EDGE,{"derivedFrom":sQuery(id+"F64.wireOp",EDGE,"E129.0")}),-1.0]])]});
            var Q1;
            Q1=makeQuery(id+"F64.imprint","IMPRINT",FACE,{"disambiguationData":[TD([[makeQuery(id+"F64.imprint","IMPRINT",EDGE,{"derivedFrom":sQuery(id+"F64.wireOp",EDGE,"E131")}),-1.0]])]});
            var Q2;
            Q2=makeQuery(id+"F64.imprint","IMPRINT",FACE,{"disambiguationData":[TD([[makeQuery(id+"F64.imprint","IMPRINT",EDGE,{"derivedFrom":sQuery(id+"F64.wireOp",EDGE,"E131")}),1.0]])]});
            var Q3;
            Q3=makeQuery(id+"F64.imprint","IMPRINT",FACE,{"disambiguationData":[TD([[makeQuery(id+"F64.imprint","IMPRINT",EDGE,{"derivedFrom":sQuery(id+"F64.wireOp",EDGE,"E129.0")}),1.0]])]});
            extrude(context, id + "F66", {"entities" : qUnion([Q0, Q1, Q2, Q3]), "operationType" : NewBodyOperationType.ADD, "depth" : 3 * mm});
        }
        {
            var Q0;
            Q0=makeQuery(id+"F66.opExtrude","CAP_FACE",FACE,{"disambiguationData":[OSD([sQuery(id+"F64.wireOp",EDGE,"E130")])],"isStart":false});
            var sketch = newSketch(context, id + "F67", { "sketchPlane" : qUnion([Q0])});
            skLineSegment(sketch, "E133.0", {"start": v(2.5, 92.14) * mm, "end": v(3.75, 91.42) * mm});
            skLineSegment(sketch, "E133.1", {"start": v(1.25, 91.42) * mm, "end": v(2.5, 92.14) * mm});
            skLineSegment(sketch, "E133.2", {"start": v(1.25, 89.98) * mm, "end": v(1.25, 91.42) * mm});
            skLineSegment(sketch, "E133.3", {"start": v(2.5, 89.26) * mm, "end": v(1.25, 89.98) * mm});
            skLineSegment(sketch, "E133.4", {"start": v(3.75, 89.98) * mm, "end": v(2.5, 89.26) * mm});
            skLineSegment(sketch, "E133.5", {"start": v(3.75, 91.42) * mm, "end": v(3.75, 89.98) * mm});
            skSolve(sketch);
        }
        {
            var Q0;
            Q0=makeQuery(id+"F67.imprint","IMPRINT",FACE,{"disambiguationData":[TD([[makeQuery(id+"F67.imprint","IMPRINT",EDGE,{"derivedFrom":sQuery(id+"F67.wireOp",EDGE,"E133.0")}),-1.0]])]});
            extrude(context, id + "F68", {"entities" : qUnion([Q0]), "operationType" : NewBodyOperationType.REMOVE, "oppositeDirection" : true, "depth" : 1 * mm});
        }
        {
            var Q0;
            Q0=makeQuery(id+"F66.opExtrude","CAP_EDGE",EDGE,{"disambiguationData":[OSD([sQuery(id+"F64.wireOp",EDGE,"E130")])],"isStart":false});
            chamfer(context, id + "F69", {"entities" : qUnion([Q0]), "width" : 0.2 * mm, "tangentPropagation" : true});
        }
        {
            var Q0;
            Q0=makeQuery(id+"F66.boolean.opBoolean","SPLIT",FACE,{"disambiguationData":[TD([makeQuery(id+"F65.opExtrude","SWEPT_FACE",FACE,{"disambiguationData":[OSD([sQuery(id+"F64.wireOp",EDGE,"E131")])]})])],"derivedFrom":makeQuery(id+"F66.opExtrude","CAP_FACE",FACE,{"disambiguationData":[OSD([sQuery(id+"F64.wireOp",EDGE,"E130")])],"isStart":true})});
            extrude(context, id + "F70", {"entities" : qUnion([Q0]), "operationType" : NewBodyOperationType.REMOVE, "oppositeDirection" : true, "depth" : 1 * mm});
        }
        {
            var Q0;
            Q0=makeQuery(id+"F65.opExtrude","CAP_EDGE",EDGE,{"disambiguationData":[OSD([sQuery(id+"F64.wireOp",EDGE,"E129.0")])],"isStart":false});
            chamfer(context, id + "F71", {"entities" : qUnion([Q0]), "width" : 0.2 * mm, "tangentPropagation" : true});
        }
        {
            var Q0;
            Q0=makeQuery(id+"F1.opExtrude","SWEPT_FACE",FACE,{"disambiguationData":[OSD([sQuery(id+"F0.wireOp",EDGE,"E2")])]});
            var sketch = newSketch(context, id + "F72", { "sketchPlane" : qUnion([Q0])});
            skCircle(sketch, "E134.0", {"center": v(2.5, 24) * mm, "radius": 1.5 * mm});
            skCircle(sketch, "E135", {"center": v(2.5, 24) * mm, "radius": 1 * mm});
            skSolve(sketch);
        }
        {
            var Q0;
            Q0=makeQuery(id+"F72.imprint","IMPRINT",FACE,{"disambiguationData":[TD([[makeQuery(id+"F72.imprint","IMPRINT",EDGE,{"derivedFrom":sQuery(id+"F72.wireOp",EDGE,"E134.0")}),1.0]])]});
            extrude(context, id + "F73", {"entities" : qUnion([Q0]), "depth" : 7 * mm});
        }
        {
            var Q0;
            Q0=makeQuery(id+"F73.opExtrude","CAP_FACE",FACE,{"disambiguationData":[OSD([sQuery(id+"F72.wireOp",EDGE,"E134.0"),sQuery(id+"F72.wireOp",EDGE,"E135")])],"isStart":false});
            var sketch = newSketch(context, id + "F74", { "sketchPlane" : qUnion([Q0])});
            skCircle(sketch, "E136", {"center": v(2.5, 24) * mm, "radius": 2.25 * mm});
            skSolve(sketch);
        }
        {
            var Q0;
            Q0=makeQuery(id+"F74.imprint","IMPRINT",FACE,{"disambiguationData":[TD([[makeQuery(id+"F74.imprint","IMPRINT",EDGE,{"derivedFrom":sQuery(id+"F74.wireOp",EDGE,"E136")}),1.0]])]});
            var Q1;
            Q1=makeQuery(id+"F74.imprint","IMPRINT",FACE,{"disambiguationData":[TD([[makeQuery(id+"F74.imprint","IMPRINT",EDGE,{"derivedFrom":makeQuery(id+"F73.opExtrude","CAP_EDGE",EDGE,{"disambiguationData":[OSD([sQuery(id+"F72.wireOp",EDGE,"E134.0")])],"isStart":false})}),1.0]])]});
            var Q2;
            Q2=makeQuery(id+"F74.imprint","IMPRINT",FACE,{"disambiguationData":[TD([[makeQuery(id+"F74.imprint","IMPRINT",EDGE,{"derivedFrom":makeQuery(id+"F73.opExtrude","CAP_EDGE",EDGE,{"disambiguationData":[OSD([sQuery(id+"F72.wireOp",EDGE,"E135")])],"isStart":false})}),1.0]])]});
            extrude(context, id + "F75", {"entities" : qUnion([Q0, Q1, Q2]), "operationType" : NewBodyOperationType.ADD, "depth" : 3 * mm});
        }
        {
            var Q0;
            Q0=makeQuery(id+"F75.opExtrude","CAP_FACE",FACE,{"disambiguationData":[OSD([sQuery(id+"F74.wireOp",EDGE,"E136")])],"isStart":false});
            var sketch = newSketch(context, id + "F76", { "sketchPlane" : qUnion([Q0])});
            skCircle(sketch, "E137.cCircle", {"center": v(2.5, 24) * mm, "radius": 1.25 * mm, "construction": true});
            skLineSegment(sketch, "E137.0", {"start": v(1.25, 23.28) * mm, "end": v(1.25, 24.72) * mm});
            skLineSegment(sketch, "E137.1", {"start": v(1.25, 24.72) * mm, "end": v(2.5, 25.44) * mm});
            skLineSegment(sketch, "E137.2", {"start": v(2.5, 25.44) * mm, "end": v(3.75, 24.72) * mm});
            skLineSegment(sketch, "E137.3", {"start": v(3.75, 24.72) * mm, "end": v(3.75, 23.28) * mm});
            skLineSegment(sketch, "E137.4", {"start": v(3.75, 23.28) * mm, "end": v(2.5, 22.56) * mm});
            skLineSegment(sketch, "E137.5", {"start": v(2.5, 22.56) * mm, "end": v(1.25, 23.28) * mm});
            skPoint(sketch, "E137.0.midPoint", {"position": v(1.25, 24) * mm});
            skSolve(sketch);
        }
        {
            var Q0;
            Q0=makeQuery(id+"F76.imprint","IMPRINT",FACE,{"disambiguationData":[TD([[makeQuery(id+"F76.imprint","IMPRINT",EDGE,{"derivedFrom":sQuery(id+"F76.wireOp",EDGE,"E137.0")}),-1.0]])]});
            extrude(context, id + "F77", {"entities" : qUnion([Q0]), "operationType" : NewBodyOperationType.REMOVE, "oppositeDirection" : true, "depth" : 1 * mm});
        }
        {
            var Q0;
            Q0=makeQuery(id+"F75.opExtrude","CAP_EDGE",EDGE,{"disambiguationData":[OSD([sQuery(id+"F74.wireOp",EDGE,"E136")])],"isStart":false});
            var Q1;
            Q1=makeQuery(id+"F73.opExtrude","CAP_EDGE",EDGE,{"disambiguationData":[OSD([sQuery(id+"F72.wireOp",EDGE,"E134.0")])],"isStart":true});
            chamfer(context, id + "F78", {"entities" : qUnion([Q0, Q1]), "width" : 0.2 * mm, "tangentPropagation" : true});
        }
        {
            var Q0;
            Q0=makeQuery(id+"F1.opExtrude","SWEPT_FACE",FACE,{"disambiguationData":[OSD([sQuery(id+"F0.wireOp",EDGE,"E3")])]});
            var sketch = newSketch(context, id + "F79", { "sketchPlane" : qUnion([Q0])});
            skCircle(sketch, "E138.0", {"center": v(-2.5, 70.4) * mm, "radius": 1.5 * mm});
            skCircle(sketch, "E139", {"center": v(-2.5, 70.4) * mm, "radius": 1 * mm});
            skSolve(sketch);
        }
        {
            var Q0;
            Q0=makeQuery(id+"F79.imprint","IMPRINT",FACE,{"disambiguationData":[TD([[makeQuery(id+"F79.imprint","IMPRINT",EDGE,{"derivedFrom":sQuery(id+"F79.wireOp",EDGE,"E138.0")}),1.0]])]});
            extrude(context, id + "F80", {"entities" : qUnion([Q0]), "depth" : 5 * mm});
        }
        {
            var Q0;
            Q0=makeQuery(id+"F80.opExtrude","CAP_FACE",FACE,{"disambiguationData":[OSD([sQuery(id+"F79.wireOp",EDGE,"E138.0"),sQuery(id+"F79.wireOp",EDGE,"E139")])],"isStart":false});
            var sketch = newSketch(context, id + "F81", { "sketchPlane" : qUnion([Q0])});
            skCircle(sketch, "E140", {"center": v(-2.5, 70.4) * mm, "radius": 2.25 * mm});
            skSolve(sketch);
        }
        {
            var Q0;
            Q0=makeQuery(id+"F81.imprint","IMPRINT",FACE,{"disambiguationData":[TD([[makeQuery(id+"F81.imprint","IMPRINT",EDGE,{"derivedFrom":makeQuery(id+"F80.opExtrude","CAP_EDGE",EDGE,{"disambiguationData":[OSD([sQuery(id+"F79.wireOp",EDGE,"E139")])],"isStart":false})}),1.0]])]});
            extrude(context, id + "F82", {"entities" : qUnion([Q0]), "operationType" : NewBodyOperationType.ADD, "oppositeDirection" : true, "depth" : 1 * mm});
        }
        {
            var Q0;
            Q0=makeQuery(id+"F81.imprint","IMPRINT",FACE,{"disambiguationData":[TD([[makeQuery(id+"F81.imprint","IMPRINT",EDGE,{"derivedFrom":sQuery(id+"F81.wireOp",EDGE,"E140")}),1.0]])]});
            var Q1;
            Q1=makeQuery(id+"F81.imprint","IMPRINT",FACE,{"disambiguationData":[TD([[makeQuery(id+"F81.imprint","IMPRINT",EDGE,{"derivedFrom":makeQuery(id+"F80.opExtrude","CAP_EDGE",EDGE,{"disambiguationData":[OSD([sQuery(id+"F79.wireOp",EDGE,"E138.0")])],"isStart":false})}),1.0]])]});
            var Q2;
            Q2=makeQuery(id+"F81.imprint","IMPRINT",FACE,{"disambiguationData":[TD([[makeQuery(id+"F81.imprint","IMPRINT",EDGE,{"derivedFrom":makeQuery(id+"F80.opExtrude","CAP_EDGE",EDGE,{"disambiguationData":[OSD([sQuery(id+"F79.wireOp",EDGE,"E139")])],"isStart":false})}),1.0]])]});
            extrude(context, id + "F83", {"entities" : qUnion([Q0, Q1, Q2]), "operationType" : NewBodyOperationType.ADD, "depth" : 2 * mm});
        }
        {
            var Q0;
            Q0=makeQuery(id+"F83.opExtrude","CAP_FACE",FACE,{"disambiguationData":[OSD([sQuery(id+"F81.wireOp",EDGE,"E140")])],"isStart":false});
            var sketch = newSketch(context, id + "F84", { "sketchPlane" : qUnion([Q0])});
            skCircle(sketch, "E141.cCircle", {"center": v(-2.5, 70.4) * mm, "radius": 1.25 * mm, "construction": true});
            skLineSegment(sketch, "E141.0", {"start": v(-3.75, 69.68) * mm, "end": v(-3.75, 71.12) * mm});
            skLineSegment(sketch, "E141.1", {"start": v(-3.75, 71.12) * mm, "end": v(-2.5, 71.84) * mm});
            skLineSegment(sketch, "E141.2", {"start": v(-2.5, 71.84) * mm, "end": v(-1.25, 71.12) * mm});
            skLineSegment(sketch, "E141.3", {"start": v(-1.25, 71.12) * mm, "end": v(-1.25, 69.68) * mm});
            skLineSegment(sketch, "E141.4", {"start": v(-1.25, 69.68) * mm, "end": v(-2.5, 68.96) * mm});
            skLineSegment(sketch, "E141.5", {"start": v(-2.5, 68.96) * mm, "end": v(-3.75, 69.68) * mm});
            skPoint(sketch, "E141.0.midPoint", {"position": v(-3.75, 70.4) * mm});
            skSolve(sketch);
        }
        {
            var Q0;
            Q0=makeQuery(id+"F84.imprint","IMPRINT",FACE,{"disambiguationData":[TD([[makeQuery(id+"F84.imprint","IMPRINT",EDGE,{"derivedFrom":sQuery(id+"F84.wireOp",EDGE,"E141.0")}),-1.0]])]});
            extrude(context, id + "F85", {"entities" : qUnion([Q0]), "operationType" : NewBodyOperationType.REMOVE, "oppositeDirection" : true, "depth" : 1 * mm});
        }
        {
            var Q0;
            Q0=makeQuery(id+"F80.opExtrude","CAP_EDGE",EDGE,{"disambiguationData":[OSD([sQuery(id+"F79.wireOp",EDGE,"E138.0")])],"isStart":true});
            var Q1;
            Q1=makeQuery(id+"F83.opExtrude","CAP_EDGE",EDGE,{"disambiguationData":[OSD([sQuery(id+"F81.wireOp",EDGE,"E140")])],"isStart":false});
            chamfer(context, id + "F86", {"entities" : qUnion([Q0, Q1]), "width" : 0.2 * mm, "tangentPropagation" : true});
        }
        {
            var Q0;
            Q0=makeQuery(id+"F16.opExtrude","SWEPT_FACE",FACE,{"disambiguationData":[OSD([sQuery(id+"F0.wireOp",EDGE,"E3")])]});
            var sketch = newSketch(context, id + "F87", { "sketchPlane" : qUnion([Q0])});
            skCircle(sketch, "E142.0", {"center": v(-2.5, 43) * mm, "radius": 1.5 * mm});
            skCircle(sketch, "E143", {"center": v(-2.5, 43) * mm, "radius": 1 * mm});
            skSolve(sketch);
        }
        {
            var Q0;
            Q0=makeQuery(id+"F87.imprint","IMPRINT",FACE,{"disambiguationData":[TD([[makeQuery(id+"F87.imprint","IMPRINT",EDGE,{"derivedFrom":sQuery(id+"F87.wireOp",EDGE,"E142.0")}),1.0]])]});
            extrude(context, id + "F88", {"entities" : qUnion([Q0]), "depth" : 3 * mm});
        }
        {
            var Q0;
            Q0=makeQuery(id+"F88.opExtrude","CAP_FACE",FACE,{"disambiguationData":[OSD([sQuery(id+"F87.wireOp",EDGE,"E142.0"),sQuery(id+"F87.wireOp",EDGE,"E143")])],"isStart":false});
            var sketch = newSketch(context, id + "F89", { "sketchPlane" : qUnion([Q0])});
            skCircle(sketch, "E144", {"center": v(-2.5, 43) * mm, "radius": 2.25 * mm});
            skSolve(sketch);
        }
        {
            var Q0;
            Q0=makeQuery(id+"F89.imprint","IMPRINT",FACE,{"disambiguationData":[TD([[makeQuery(id+"F89.imprint","IMPRINT",EDGE,{"derivedFrom":makeQuery(id+"F88.opExtrude","CAP_EDGE",EDGE,{"disambiguationData":[OSD([sQuery(id+"F87.wireOp",EDGE,"E143")])],"isStart":false})}),1.0]])]});
            extrude(context, id + "F90", {"entities" : qUnion([Q0]), "operationType" : NewBodyOperationType.ADD, "oppositeDirection" : true, "depth" : 1 * mm});
        }
        {
            var Q0;
            Q0=makeQuery(id+"F89.imprint","IMPRINT",FACE,{"disambiguationData":[TD([[makeQuery(id+"F89.imprint","IMPRINT",EDGE,{"derivedFrom":sQuery(id+"F89.wireOp",EDGE,"E144")}),1.0]])]});
            var Q1;
            Q1=makeQuery(id+"F89.imprint","IMPRINT",FACE,{"disambiguationData":[TD([[makeQuery(id+"F89.imprint","IMPRINT",EDGE,{"derivedFrom":makeQuery(id+"F88.opExtrude","CAP_EDGE",EDGE,{"disambiguationData":[OSD([sQuery(id+"F87.wireOp",EDGE,"E142.0")])],"isStart":false})}),1.0]])]});
            var Q2;
            Q2=makeQuery(id+"F89.imprint","IMPRINT",FACE,{"disambiguationData":[TD([[makeQuery(id+"F89.imprint","IMPRINT",EDGE,{"derivedFrom":makeQuery(id+"F88.opExtrude","CAP_EDGE",EDGE,{"disambiguationData":[OSD([sQuery(id+"F87.wireOp",EDGE,"E143")])],"isStart":false})}),1.0]])]});
            extrude(context, id + "F91", {"entities" : qUnion([Q0, Q1, Q2]), "operationType" : NewBodyOperationType.ADD, "depth" : 2 * mm});
        }
        {
            var Q0;
            Q0=makeQuery(id+"F91.opExtrude","CAP_FACE",FACE,{"disambiguationData":[OSD([sQuery(id+"F89.wireOp",EDGE,"E144")])],"isStart":false});
            var sketch = newSketch(context, id + "F92", { "sketchPlane" : qUnion([Q0])});
            skCircle(sketch, "E145.cCircle", {"center": v(-2.5, 43) * mm, "radius": 1.25 * mm, "construction": true});
            skLineSegment(sketch, "E145.0", {"start": v(-1.78, 41.75) * mm, "end": v(-3.22, 41.75) * mm});
            skLineSegment(sketch, "E145.1", {"start": v(-3.22, 41.75) * mm, "end": v(-3.94, 43) * mm});
            skLineSegment(sketch, "E145.2", {"start": v(-3.94, 43) * mm, "end": v(-3.22, 44.25) * mm});
            skLineSegment(sketch, "E145.3", {"start": v(-3.22, 44.25) * mm, "end": v(-1.78, 44.25) * mm});
            skLineSegment(sketch, "E145.4", {"start": v(-1.78, 44.25) * mm, "end": v(-1.06, 43) * mm});
            skLineSegment(sketch, "E145.5", {"start": v(-1.06, 43) * mm, "end": v(-1.78, 41.75) * mm});
            skPoint(sketch, "E145.0.midPoint", {"position": v(-2.5, 41.75) * mm});
            skSolve(sketch);
        }
        {
            var Q0;
            Q0=makeQuery(id+"F92.imprint","IMPRINT",FACE,{"disambiguationData":[TD([[makeQuery(id+"F92.imprint","IMPRINT",EDGE,{"derivedFrom":sQuery(id+"F92.wireOp",EDGE,"E145.0")}),-1.0]])]});
            extrude(context, id + "F93", {"entities" : qUnion([Q0]), "operationType" : NewBodyOperationType.REMOVE, "oppositeDirection" : true, "depth" : 1 * mm});
        }
        {
            var Q0;
            Q0=makeQuery(id+"F88.opExtrude","CAP_EDGE",EDGE,{"disambiguationData":[OSD([sQuery(id+"F87.wireOp",EDGE,"E142.0")])],"isStart":true});
            var Q1;
            Q1=makeQuery(id+"F91.opExtrude","CAP_EDGE",EDGE,{"disambiguationData":[OSD([sQuery(id+"F89.wireOp",EDGE,"E144")])],"isStart":false});
            chamfer(context, id + "F94", {"entities" : qUnion([Q0, Q1]), "width" : 0.2 * mm, "tangentPropagation" : true});
        }
    });
